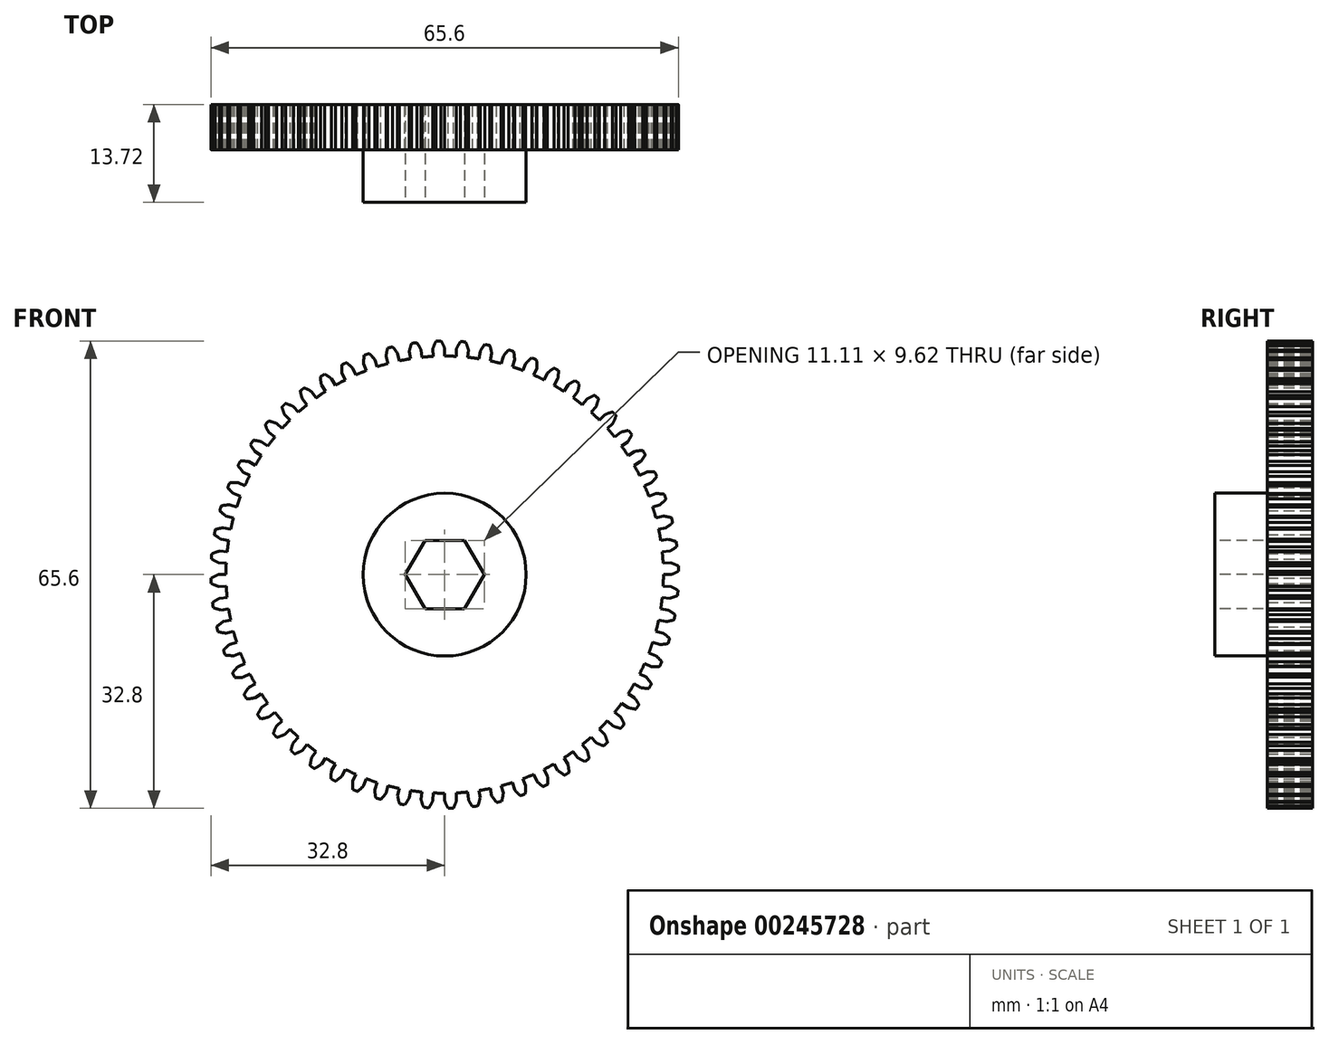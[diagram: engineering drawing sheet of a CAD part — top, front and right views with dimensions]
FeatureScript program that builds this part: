
annotation { "Feature Type Name" : "Feature", "Feature Type Description" : "" }
export const myFeature = defineFeature(function(context is Context, id is Id, definition is map)
    precondition{}
    {
        {
            var Q0;
            Q0=qCreatedBy(makeId("Front.planeOp"),FACE);
            var sketch = newSketch(context, id + "F0", { "sketchPlane" : qUnion([Q0])});
            skCircle(sketch, "E0", {"center": v(0, 0) * mm, "radius": 30.7 * mm});
            skLineSegment(sketch, "E1", {"start": v(0, 30.7) * mm, "end": v(0, 31.75) * mm});
            skLineSegment(sketch, "E2", {"start": v(-0.8, 30.68) * mm, "end": v(-0.86, 32.8) * mm, "construction": true});
            skArc(sketch, "E3.trimOffspring", {"start": v(-0.5, 32.8) * mm, "mid": v(-0.68, 32.8) * mm, "end": v(-0.86, 32.8) * mm});
            skArc(sketch, "E4.trimOffspring", {"start": v(0, 31.75) * mm, "mid": v(-0.23, 32.29) * mm, "end": v(-0.5, 32.8) * mm});
            skArc(sketch, "E5.MirrorCS", {"start": v(-1.22, 32.79) * mm, "mid": v(-1.04, 32.8) * mm, "end": v(-0.86, 32.8) * mm});
            skArc(sketch, "E6.MirrorCS", {"start": v(-1.66, 31.7) * mm, "mid": v(-1.46, 32.25) * mm, "end": v(-1.22, 32.79) * mm});
            skLineSegment(sketch, "E7.MirrorCS", {"start": v(-1.6, 30.65) * mm, "end": v(-1.66, 31.7) * mm});
            skLineSegment(sketch, "E8.1.0", {"start": v(-4, 30.43) * mm, "end": v(-4.28, 32.53) * mm, "construction": true});
            skLineSegment(sketch, "E8.1.1", {"start": v(-3.2, 30.52) * mm, "end": v(-3.32, 31.58) * mm});
            skLineSegment(sketch, "E8.1.2", {"start": v(-4.8, 30.31) * mm, "end": v(-4.97, 31.36) * mm});
            skArc(sketch, "E8.1.3", {"start": v(-4.97, 31.36) * mm, "mid": v(-4.82, 31.92) * mm, "end": v(-4.64, 32.48) * mm});
            skArc(sketch, "E8.1.4", {"start": v(-3.32, 31.58) * mm, "mid": v(-3.6, 32.09) * mm, "end": v(-3.92, 32.57) * mm});
            skArc(sketch, "E8.1.5", {"start": v(-3.92, 32.57) * mm, "mid": v(-4.1, 32.55) * mm, "end": v(-4.28, 32.53) * mm});
            skArc(sketch, "E8.1.6", {"start": v(-4.64, 32.48) * mm, "mid": v(-4.46, 32.5) * mm, "end": v(-4.28, 32.53) * mm});
            skLineSegment(sketch, "E8.2.0", {"start": v(-7.16, 29.84) * mm, "end": v(-7.66, 31.9) * mm, "construction": true});
            skLineSegment(sketch, "E8.2.1", {"start": v(-6.38, 30.02) * mm, "end": v(-6.6, 31.06) * mm});
            skLineSegment(sketch, "E8.2.2", {"start": v(-7.94, 29.65) * mm, "end": v(-8.22, 30.67) * mm});
            skArc(sketch, "E8.2.3", {"start": v(-8.22, 30.67) * mm, "mid": v(-8.13, 31.25) * mm, "end": v(-8.01, 31.82) * mm});
            skArc(sketch, "E8.2.4", {"start": v(-6.6, 31.06) * mm, "mid": v(-6.94, 31.53) * mm, "end": v(-7.3, 31.98) * mm});
            skArc(sketch, "E8.2.5", {"start": v(-7.3, 31.98) * mm, "mid": v(-7.48, 31.94) * mm, "end": v(-7.66, 31.9) * mm});
            skArc(sketch, "E8.2.6", {"start": v(-8.01, 31.82) * mm, "mid": v(-7.83, 31.86) * mm, "end": v(-7.66, 31.9) * mm});
            skLineSegment(sketch, "E9.3.3.0", {"start": v(-9.48, 29.19) * mm, "end": v(-9.81, 30.2) * mm});
            skLineSegment(sketch, "E9.6.3.0", {"start": v(-11, 28.65) * mm, "end": v(-11.38, 29.64) * mm});
            skArc(sketch, "E9.9.3.0", {"start": v(-11.38, 29.64) * mm, "mid": v(-11.36, 30.22) * mm, "end": v(-11.3, 30.8) * mm});
            skArc(sketch, "E9.13.3.0", {"start": v(-9.81, 30.2) * mm, "mid": v(-10.2, 30.64) * mm, "end": v(-10.61, 31.05) * mm});
            skLineSegment(sketch, "E9.14.3.0", {"start": v(-10.25, 28.93) * mm, "end": v(-10.95, 30.93) * mm, "construction": true});
            skArc(sketch, "E9.17.3.0", {"start": v(-10.61, 31.05) * mm, "mid": v(-10.78, 30.99) * mm, "end": v(-10.95, 30.93) * mm});
            skArc(sketch, "E9.21.3.0", {"start": v(-11.3, 30.8) * mm, "mid": v(-11.12, 30.87) * mm, "end": v(-10.95, 30.93) * mm});
            skLineSegment(sketch, "E9.3.4.0", {"start": v(-12.48, 28.04) * mm, "end": v(-12.91, 29) * mm});
            skLineSegment(sketch, "E9.6.4.0", {"start": v(-13.93, 27.35) * mm, "end": v(-14.41, 28.29) * mm});
            skArc(sketch, "E9.9.4.0", {"start": v(-14.41, 28.29) * mm, "mid": v(-14.45, 28.87) * mm, "end": v(-14.45, 29.45) * mm});
            skArc(sketch, "E9.13.4.0", {"start": v(-12.91, 29) * mm, "mid": v(-13.34, 29.4) * mm, "end": v(-13.8, 29.77) * mm});
            skLineSegment(sketch, "E9.14.4.0", {"start": v(-13.21, 27.7) * mm, "end": v(-14.12, 29.61) * mm, "construction": true});
            skArc(sketch, "E9.17.4.0", {"start": v(-13.8, 29.77) * mm, "mid": v(-13.96, 29.69) * mm, "end": v(-14.12, 29.61) * mm});
            skArc(sketch, "E9.21.4.0", {"start": v(-14.45, 29.45) * mm, "mid": v(-14.29, 29.53) * mm, "end": v(-14.12, 29.61) * mm});
            skLineSegment(sketch, "E9.3.5.0", {"start": v(-15.35, 26.58) * mm, "end": v(-15.87, 27.5) * mm});
            skLineSegment(sketch, "E9.6.5.0", {"start": v(-16.72, 25.74) * mm, "end": v(-17.3, 26.63) * mm});
            skArc(sketch, "E9.9.5.0", {"start": v(-17.3, 26.63) * mm, "mid": v(-17.4, 27.2) * mm, "end": v(-17.45, 27.78) * mm});
            skArc(sketch, "E9.13.5.0", {"start": v(-15.88, 27.5) * mm, "mid": v(-16.34, 27.85) * mm, "end": v(-16.83, 28.16) * mm});
            skLineSegment(sketch, "E9.14.5.0", {"start": v(-16.04, 26.17) * mm, "end": v(-17.14, 27.97) * mm, "construction": true});
            skArc(sketch, "E9.17.5.0", {"start": v(-16.83, 28.16) * mm, "mid": v(-16.99, 28.07) * mm, "end": v(-17.14, 27.97) * mm});
            skArc(sketch, "E9.21.5.0", {"start": v(-17.45, 27.78) * mm, "mid": v(-17.3, 27.88) * mm, "end": v(-17.14, 27.97) * mm});
            skLineSegment(sketch, "E9.3.6.0", {"start": v(-18.04, 24.83) * mm, "end": v(-18.66, 25.69) * mm});
            skLineSegment(sketch, "E9.6.6.0", {"start": v(-19.31, 23.85) * mm, "end": v(-19.98, 24.67) * mm});
            skArc(sketch, "E9.9.6.0", {"start": v(-19.98, 24.67) * mm, "mid": v(-20.14, 25.24) * mm, "end": v(-20.26, 25.8) * mm});
            skArc(sketch, "E9.13.6.0", {"start": v(-18.66, 25.69) * mm, "mid": v(-19.16, 25.99) * mm, "end": v(-19.68, 26.25) * mm});
            skLineSegment(sketch, "E9.14.6.0", {"start": v(-18.68, 24.35) * mm, "end": v(-19.97, 26.03) * mm, "construction": true});
            skArc(sketch, "E9.17.6.0", {"start": v(-19.68, 26.25) * mm, "mid": v(-19.83, 26.14) * mm, "end": v(-19.97, 26.03) * mm});
            skArc(sketch, "E9.21.6.0", {"start": v(-20.26, 25.8) * mm, "mid": v(-20.12, 25.92) * mm, "end": v(-19.97, 26.03) * mm});
            skLineSegment(sketch, "E9.3.7.0", {"start": v(-20.54, 22.8) * mm, "end": v(-21.24, 23.6) * mm});
            skLineSegment(sketch, "E9.6.7.0", {"start": v(-21.7, 21.7) * mm, "end": v(-22.45, 22.45) * mm});
            skArc(sketch, "E9.9.7.0", {"start": v(-22.45, 22.45) * mm, "mid": v(-22.67, 23) * mm, "end": v(-22.84, 23.55) * mm});
            skArc(sketch, "E9.13.7.0", {"start": v(-21.24, 23.6) * mm, "mid": v(-21.77, 23.84) * mm, "end": v(-22.32, 24.05) * mm});
            skLineSegment(sketch, "E9.14.7.0", {"start": v(-21.13, 22.26) * mm, "end": v(-22.58, 23.8) * mm, "construction": true});
            skArc(sketch, "E9.17.7.0", {"start": v(-22.32, 24.05) * mm, "mid": v(-22.45, 23.92) * mm, "end": v(-22.58, 23.8) * mm});
            skArc(sketch, "E9.21.7.0", {"start": v(-22.84, 23.55) * mm, "mid": v(-22.71, 23.67) * mm, "end": v(-22.58, 23.8) * mm});
            skLineSegment(sketch, "E9.3.8.0", {"start": v(-22.8, 20.54) * mm, "end": v(-23.6, 21.24) * mm});
            skLineSegment(sketch, "E9.6.8.0", {"start": v(-23.85, 19.31) * mm, "end": v(-24.67, 19.98) * mm});
            skArc(sketch, "E9.9.8.0", {"start": v(-24.67, 19.98) * mm, "mid": v(-24.95, 20.5) * mm, "end": v(-25.18, 21.03) * mm});
            skArc(sketch, "E9.13.8.0", {"start": v(-23.6, 21.24) * mm, "mid": v(-24.15, 21.43) * mm, "end": v(-24.71, 21.58) * mm});
            skLineSegment(sketch, "E9.14.8.0", {"start": v(-23.34, 19.93) * mm, "end": v(-24.95, 21.3) * mm, "construction": true});
            skArc(sketch, "E9.17.8.0", {"start": v(-24.71, 21.58) * mm, "mid": v(-24.83, 21.44) * mm, "end": v(-24.95, 21.3) * mm});
            skArc(sketch, "E9.21.8.0", {"start": v(-25.18, 21.03) * mm, "mid": v(-25.06, 21.17) * mm, "end": v(-24.95, 21.3) * mm});
            skLineSegment(sketch, "E9.3.9.0", {"start": v(-24.83, 18.04) * mm, "end": v(-25.69, 18.66) * mm});
            skLineSegment(sketch, "E9.6.9.0", {"start": v(-25.74, 16.72) * mm, "end": v(-26.63, 17.3) * mm});
            skArc(sketch, "E9.9.9.0", {"start": v(-26.63, 17.3) * mm, "mid": v(-26.95, 17.78) * mm, "end": v(-27.24, 18.28) * mm});
            skArc(sketch, "E9.13.9.0", {"start": v(-25.69, 18.66) * mm, "mid": v(-26.26, 18.8) * mm, "end": v(-26.83, 18.88) * mm});
            skLineSegment(sketch, "E9.14.9.0", {"start": v(-25.3, 17.38) * mm, "end": v(-27.04, 18.58) * mm, "construction": true});
            skArc(sketch, "E9.17.9.0", {"start": v(-26.83, 18.88) * mm, "mid": v(-26.94, 18.73) * mm, "end": v(-27.04, 18.58) * mm});
            skArc(sketch, "E9.21.9.0", {"start": v(-27.24, 18.28) * mm, "mid": v(-27.14, 18.43) * mm, "end": v(-27.04, 18.58) * mm});
            skLineSegment(sketch, "E9.3.10.0", {"start": v(-26.58, 15.35) * mm, "end": v(-27.5, 15.88) * mm});
            skLineSegment(sketch, "E9.6.10.0", {"start": v(-27.35, 13.93) * mm, "end": v(-28.29, 14.41) * mm});
            skArc(sketch, "E9.9.10.0", {"start": v(-28.29, 14.41) * mm, "mid": v(-28.66, 14.86) * mm, "end": v(-29, 15.34) * mm});
            skArc(sketch, "E9.13.10.0", {"start": v(-27.5, 15.88) * mm, "mid": v(-28.08, 15.94) * mm, "end": v(-28.66, 15.97) * mm});
            skLineSegment(sketch, "E9.14.10.0", {"start": v(-26.97, 14.64) * mm, "end": v(-28.83, 15.65) * mm, "construction": true});
            skArc(sketch, "E9.17.10.0", {"start": v(-28.66, 15.97) * mm, "mid": v(-28.75, 15.81) * mm, "end": v(-28.83, 15.65) * mm});
            skArc(sketch, "E9.21.10.0", {"start": v(-29, 15.34) * mm, "mid": v(-28.92, 15.5) * mm, "end": v(-28.83, 15.65) * mm});
            skLineSegment(sketch, "E9.3.11.0", {"start": v(-28.04, 12.48) * mm, "end": v(-29, 12.91) * mm});
            skLineSegment(sketch, "E9.6.11.0", {"start": v(-28.65, 11) * mm, "end": v(-29.64, 11.38) * mm});
            skArc(sketch, "E9.9.11.0", {"start": v(-29.64, 11.38) * mm, "mid": v(-30.06, 11.78) * mm, "end": v(-30.45, 12.22) * mm});
            skArc(sketch, "E9.13.11.0", {"start": v(-29, 12.91) * mm, "mid": v(-29.59, 12.92) * mm, "end": v(-30.17, 12.89) * mm});
            skLineSegment(sketch, "E9.14.11.0", {"start": v(-28.36, 11.75) * mm, "end": v(-30.31, 12.56) * mm, "construction": true});
            skArc(sketch, "E9.17.11.0", {"start": v(-30.17, 12.89) * mm, "mid": v(-30.24, 12.72) * mm, "end": v(-30.31, 12.56) * mm});
            skArc(sketch, "E9.21.11.0", {"start": v(-30.45, 12.22) * mm, "mid": v(-30.38, 12.39) * mm, "end": v(-30.31, 12.56) * mm});
            skLineSegment(sketch, "E9.3.12.0", {"start": v(-29.19, 9.48) * mm, "end": v(-30.2, 9.81) * mm});
            skLineSegment(sketch, "E9.6.12.0", {"start": v(-29.65, 7.94) * mm, "end": v(-30.67, 8.22) * mm});
            skArc(sketch, "E9.9.12.0", {"start": v(-30.67, 8.22) * mm, "mid": v(-31.13, 8.58) * mm, "end": v(-31.56, 8.97) * mm});
            skArc(sketch, "E9.13.12.0", {"start": v(-30.2, 9.81) * mm, "mid": v(-30.78, 9.76) * mm, "end": v(-31.35, 9.66) * mm});
            skLineSegment(sketch, "E9.14.12.0", {"start": v(-29.43, 8.72) * mm, "end": v(-31.46, 9.32) * mm, "construction": true});
            skArc(sketch, "E9.17.12.0", {"start": v(-31.35, 9.66) * mm, "mid": v(-31.4, 9.5) * mm, "end": v(-31.46, 9.32) * mm});
            skArc(sketch, "E9.21.12.0", {"start": v(-31.56, 8.97) * mm, "mid": v(-31.5, 9.14) * mm, "end": v(-31.46, 9.32) * mm});
            skLineSegment(sketch, "E9.3.13.0", {"start": v(-30.02, 6.38) * mm, "end": v(-31.06, 6.6) * mm});
            skLineSegment(sketch, "E9.6.13.0", {"start": v(-30.31, 4.8) * mm, "end": v(-31.36, 4.97) * mm});
            skArc(sketch, "E9.9.13.0", {"start": v(-31.36, 4.97) * mm, "mid": v(-31.85, 5.28) * mm, "end": v(-32.32, 5.62) * mm});
            skArc(sketch, "E9.13.13.0", {"start": v(-31.06, 6.6) * mm, "mid": v(-31.63, 6.49) * mm, "end": v(-32.2, 6.33) * mm});
            skLineSegment(sketch, "E9.14.13.0", {"start": v(-30.18, 5.6) * mm, "end": v(-32.26, 5.98) * mm, "construction": true});
            skArc(sketch, "E9.17.13.0", {"start": v(-32.2, 6.33) * mm, "mid": v(-32.23, 6.16) * mm, "end": v(-32.26, 5.98) * mm});
            skArc(sketch, "E9.21.13.0", {"start": v(-32.32, 5.62) * mm, "mid": v(-32.3, 5.8) * mm, "end": v(-32.26, 5.98) * mm});
            skLineSegment(sketch, "E9.3.14.0", {"start": v(-30.52, 3.2) * mm, "end": v(-31.58, 3.32) * mm});
            skLineSegment(sketch, "E9.6.14.0", {"start": v(-30.65, 1.6) * mm, "end": v(-31.7, 1.66) * mm});
            skArc(sketch, "E9.9.14.0", {"start": v(-31.7, 1.66) * mm, "mid": v(-32.23, 1.92) * mm, "end": v(-32.73, 2.21) * mm});
            skArc(sketch, "E9.13.14.0", {"start": v(-31.58, 3.32) * mm, "mid": v(-32.13, 3.15) * mm, "end": v(-32.68, 2.93) * mm});
            skLineSegment(sketch, "E9.14.14.0", {"start": v(-30.6, 2.4) * mm, "end": v(-32.7, 2.57) * mm, "construction": true});
            skArc(sketch, "E9.17.14.0", {"start": v(-32.68, 2.93) * mm, "mid": v(-32.7, 2.75) * mm, "end": v(-32.7, 2.57) * mm});
            skArc(sketch, "E9.21.14.0", {"start": v(-32.73, 2.21) * mm, "mid": v(-32.72, 2.4) * mm, "end": v(-32.7, 2.57) * mm});
            skLineSegment(sketch, "E9.3.15.0", {"start": v(-30.7, 0) * mm, "end": v(-31.75, 0) * mm});
            skLineSegment(sketch, "E9.6.15.0", {"start": v(-30.65, -1.6) * mm, "end": v(-31.7, -1.66) * mm});
            skArc(sketch, "E9.9.15.0", {"start": v(-31.7, -1.66) * mm, "mid": v(-32.25, -1.46) * mm, "end": v(-32.79, -1.22) * mm});
            skArc(sketch, "E9.13.15.0", {"start": v(-31.75, 0) * mm, "mid": v(-32.29, -0.23) * mm, "end": v(-32.8, -0.5) * mm});
            skLineSegment(sketch, "E9.14.15.0", {"start": v(-30.68, -0.8) * mm, "end": v(-32.8, -0.86) * mm, "construction": true});
            skArc(sketch, "E9.17.15.0", {"start": v(-32.8, -0.5) * mm, "mid": v(-32.8, -0.68) * mm, "end": v(-32.8, -0.86) * mm});
            skArc(sketch, "E9.21.15.0", {"start": v(-32.79, -1.22) * mm, "mid": v(-32.8, -1.04) * mm, "end": v(-32.8, -0.86) * mm});
            skLineSegment(sketch, "E9.3.16.0", {"start": v(-30.52, -3.2) * mm, "end": v(-31.58, -3.32) * mm});
            skLineSegment(sketch, "E9.6.16.0", {"start": v(-30.31, -4.8) * mm, "end": v(-31.36, -4.97) * mm});
            skArc(sketch, "E9.9.16.0", {"start": v(-31.36, -4.97) * mm, "mid": v(-31.92, -4.82) * mm, "end": v(-32.48, -4.64) * mm});
            skArc(sketch, "E9.13.16.0", {"start": v(-31.58, -3.32) * mm, "mid": v(-32.09, -3.6) * mm, "end": v(-32.57, -3.92) * mm});
            skLineSegment(sketch, "E9.14.16.0", {"start": v(-30.43, -4) * mm, "end": v(-32.53, -4.28) * mm, "construction": true});
            skArc(sketch, "E9.17.16.0", {"start": v(-32.57, -3.92) * mm, "mid": v(-32.55, -4.1) * mm, "end": v(-32.53, -4.28) * mm});
            skArc(sketch, "E9.21.16.0", {"start": v(-32.48, -4.64) * mm, "mid": v(-32.5, -4.46) * mm, "end": v(-32.53, -4.28) * mm});
            skLineSegment(sketch, "E9.3.17.0", {"start": v(-30.02, -6.38) * mm, "end": v(-31.06, -6.6) * mm});
            skLineSegment(sketch, "E9.6.17.0", {"start": v(-29.65, -7.94) * mm, "end": v(-30.67, -8.22) * mm});
            skArc(sketch, "E9.9.17.0", {"start": v(-30.67, -8.22) * mm, "mid": v(-31.25, -8.13) * mm, "end": v(-31.82, -8.01) * mm});
            skArc(sketch, "E9.13.17.0", {"start": v(-31.06, -6.6) * mm, "mid": v(-31.53, -6.94) * mm, "end": v(-31.98, -7.3) * mm});
            skLineSegment(sketch, "E9.14.17.0", {"start": v(-29.84, -7.16) * mm, "end": v(-31.9, -7.66) * mm, "construction": true});
            skArc(sketch, "E9.17.17.0", {"start": v(-31.98, -7.3) * mm, "mid": v(-31.94, -7.48) * mm, "end": v(-31.9, -7.66) * mm});
            skArc(sketch, "E9.21.17.0", {"start": v(-31.82, -8.01) * mm, "mid": v(-31.86, -7.83) * mm, "end": v(-31.9, -7.66) * mm});
            skLineSegment(sketch, "E9.3.18.0", {"start": v(-29.19, -9.48) * mm, "end": v(-30.2, -9.81) * mm});
            skLineSegment(sketch, "E9.6.18.0", {"start": v(-28.65, -11) * mm, "end": v(-29.64, -11.38) * mm});
            skArc(sketch, "E9.9.18.0", {"start": v(-29.64, -11.38) * mm, "mid": v(-30.22, -11.36) * mm, "end": v(-30.8, -11.3) * mm});
            skArc(sketch, "E9.13.18.0", {"start": v(-30.2, -9.81) * mm, "mid": v(-30.64, -10.2) * mm, "end": v(-31.05, -10.61) * mm});
            skLineSegment(sketch, "E9.14.18.0", {"start": v(-28.93, -10.25) * mm, "end": v(-30.93, -10.95) * mm, "construction": true});
            skArc(sketch, "E9.17.18.0", {"start": v(-31.05, -10.61) * mm, "mid": v(-30.99, -10.78) * mm, "end": v(-30.93, -10.95) * mm});
            skArc(sketch, "E9.21.18.0", {"start": v(-30.8, -11.3) * mm, "mid": v(-30.87, -11.12) * mm, "end": v(-30.93, -10.95) * mm});
            skLineSegment(sketch, "E9.3.19.0", {"start": v(-28.04, -12.48) * mm, "end": v(-29, -12.91) * mm});
            skLineSegment(sketch, "E9.6.19.0", {"start": v(-27.35, -13.93) * mm, "end": v(-28.29, -14.41) * mm});
            skArc(sketch, "E9.9.19.0", {"start": v(-28.29, -14.41) * mm, "mid": v(-28.87, -14.45) * mm, "end": v(-29.45, -14.45) * mm});
            skArc(sketch, "E9.13.19.0", {"start": v(-29, -12.91) * mm, "mid": v(-29.4, -13.34) * mm, "end": v(-29.77, -13.8) * mm});
            skLineSegment(sketch, "E9.14.19.0", {"start": v(-27.7, -13.21) * mm, "end": v(-29.61, -14.12) * mm, "construction": true});
            skArc(sketch, "E9.17.19.0", {"start": v(-29.77, -13.8) * mm, "mid": v(-29.69, -13.96) * mm, "end": v(-29.61, -14.12) * mm});
            skArc(sketch, "E9.21.19.0", {"start": v(-29.45, -14.45) * mm, "mid": v(-29.53, -14.29) * mm, "end": v(-29.61, -14.12) * mm});
            skLineSegment(sketch, "E9.3.20.0", {"start": v(-26.58, -15.35) * mm, "end": v(-27.5, -15.88) * mm});
            skLineSegment(sketch, "E9.6.20.0", {"start": v(-25.74, -16.72) * mm, "end": v(-26.63, -17.3) * mm});
            skArc(sketch, "E9.9.20.0", {"start": v(-26.63, -17.3) * mm, "mid": v(-27.2, -17.4) * mm, "end": v(-27.78, -17.45) * mm});
            skArc(sketch, "E9.13.20.0", {"start": v(-27.5, -15.87) * mm, "mid": v(-27.85, -16.34) * mm, "end": v(-28.16, -16.83) * mm});
            skLineSegment(sketch, "E9.14.20.0", {"start": v(-26.17, -16.04) * mm, "end": v(-27.97, -17.14) * mm, "construction": true});
            skArc(sketch, "E9.17.20.0", {"start": v(-28.16, -16.83) * mm, "mid": v(-28.07, -16.99) * mm, "end": v(-27.97, -17.14) * mm});
            skArc(sketch, "E9.21.20.0", {"start": v(-27.78, -17.45) * mm, "mid": v(-27.88, -17.3) * mm, "end": v(-27.97, -17.14) * mm});
            skLineSegment(sketch, "E9.3.21.0", {"start": v(-24.83, -18.04) * mm, "end": v(-25.69, -18.66) * mm});
            skLineSegment(sketch, "E9.6.21.0", {"start": v(-23.85, -19.31) * mm, "end": v(-24.67, -19.98) * mm});
            skArc(sketch, "E9.9.21.0", {"start": v(-24.67, -19.98) * mm, "mid": v(-25.24, -20.14) * mm, "end": v(-25.8, -20.26) * mm});
            skArc(sketch, "E9.13.21.0", {"start": v(-25.69, -18.66) * mm, "mid": v(-25.99, -19.16) * mm, "end": v(-26.25, -19.68) * mm});
            skLineSegment(sketch, "E9.14.21.0", {"start": v(-24.35, -18.68) * mm, "end": v(-26.03, -19.97) * mm, "construction": true});
            skArc(sketch, "E9.17.21.0", {"start": v(-26.25, -19.68) * mm, "mid": v(-26.14, -19.83) * mm, "end": v(-26.03, -19.97) * mm});
            skArc(sketch, "E9.21.21.0", {"start": v(-25.8, -20.26) * mm, "mid": v(-25.92, -20.12) * mm, "end": v(-26.03, -19.97) * mm});
            skLineSegment(sketch, "E9.3.22.0", {"start": v(-22.8, -20.54) * mm, "end": v(-23.6, -21.24) * mm});
            skLineSegment(sketch, "E9.6.22.0", {"start": v(-21.7, -21.7) * mm, "end": v(-22.45, -22.45) * mm});
            skArc(sketch, "E9.9.22.0", {"start": v(-22.45, -22.45) * mm, "mid": v(-23, -22.67) * mm, "end": v(-23.55, -22.84) * mm});
            skArc(sketch, "E9.13.22.0", {"start": v(-23.6, -21.24) * mm, "mid": v(-23.84, -21.77) * mm, "end": v(-24.05, -22.32) * mm});
            skLineSegment(sketch, "E9.14.22.0", {"start": v(-22.26, -21.13) * mm, "end": v(-23.8, -22.58) * mm, "construction": true});
            skArc(sketch, "E9.17.22.0", {"start": v(-24.05, -22.32) * mm, "mid": v(-23.92, -22.45) * mm, "end": v(-23.8, -22.58) * mm});
            skArc(sketch, "E9.21.22.0", {"start": v(-23.55, -22.84) * mm, "mid": v(-23.67, -22.71) * mm, "end": v(-23.8, -22.58) * mm});
            skLineSegment(sketch, "E9.3.23.0", {"start": v(-20.54, -22.8) * mm, "end": v(-21.24, -23.6) * mm});
            skLineSegment(sketch, "E9.6.23.0", {"start": v(-19.31, -23.85) * mm, "end": v(-19.98, -24.67) * mm});
            skArc(sketch, "E9.9.23.0", {"start": v(-19.98, -24.67) * mm, "mid": v(-20.5, -24.95) * mm, "end": v(-21.03, -25.18) * mm});
            skArc(sketch, "E9.13.23.0", {"start": v(-21.24, -23.6) * mm, "mid": v(-21.43, -24.15) * mm, "end": v(-21.58, -24.71) * mm});
            skLineSegment(sketch, "E9.14.23.0", {"start": v(-19.93, -23.34) * mm, "end": v(-21.3, -24.95) * mm, "construction": true});
            skArc(sketch, "E9.17.23.0", {"start": v(-21.58, -24.71) * mm, "mid": v(-21.44, -24.83) * mm, "end": v(-21.3, -24.95) * mm});
            skArc(sketch, "E9.21.23.0", {"start": v(-21.03, -25.18) * mm, "mid": v(-21.17, -25.06) * mm, "end": v(-21.3, -24.95) * mm});
            skLineSegment(sketch, "E9.3.24.0", {"start": v(-18.04, -24.83) * mm, "end": v(-18.66, -25.69) * mm});
            skLineSegment(sketch, "E9.6.24.0", {"start": v(-16.72, -25.74) * mm, "end": v(-17.3, -26.63) * mm});
            skArc(sketch, "E9.9.24.0", {"start": v(-17.3, -26.63) * mm, "mid": v(-17.78, -26.95) * mm, "end": v(-18.28, -27.24) * mm});
            skArc(sketch, "E9.13.24.0", {"start": v(-18.66, -25.69) * mm, "mid": v(-18.8, -26.26) * mm, "end": v(-18.88, -26.83) * mm});
            skLineSegment(sketch, "E9.14.24.0", {"start": v(-17.38, -25.3) * mm, "end": v(-18.58, -27.04) * mm, "construction": true});
            skArc(sketch, "E9.17.24.0", {"start": v(-18.88, -26.83) * mm, "mid": v(-18.73, -26.94) * mm, "end": v(-18.58, -27.04) * mm});
            skArc(sketch, "E9.21.24.0", {"start": v(-18.28, -27.24) * mm, "mid": v(-18.43, -27.14) * mm, "end": v(-18.58, -27.04) * mm});
            skLineSegment(sketch, "E9.3.25.0", {"start": v(-15.35, -26.58) * mm, "end": v(-15.87, -27.5) * mm});
            skLineSegment(sketch, "E9.6.25.0", {"start": v(-13.93, -27.35) * mm, "end": v(-14.41, -28.29) * mm});
            skArc(sketch, "E9.9.25.0", {"start": v(-14.41, -28.29) * mm, "mid": v(-14.86, -28.66) * mm, "end": v(-15.34, -29) * mm});
            skArc(sketch, "E9.13.25.0", {"start": v(-15.87, -27.5) * mm, "mid": v(-15.94, -28.08) * mm, "end": v(-15.97, -28.66) * mm});
            skLineSegment(sketch, "E9.14.25.0", {"start": v(-14.64, -26.97) * mm, "end": v(-15.65, -28.83) * mm, "construction": true});
            skArc(sketch, "E9.17.25.0", {"start": v(-15.97, -28.66) * mm, "mid": v(-15.81, -28.75) * mm, "end": v(-15.65, -28.83) * mm});
            skArc(sketch, "E9.21.25.0", {"start": v(-15.34, -29) * mm, "mid": v(-15.5, -28.92) * mm, "end": v(-15.65, -28.83) * mm});
            skLineSegment(sketch, "E9.3.26.0", {"start": v(-12.48, -28.04) * mm, "end": v(-12.91, -29) * mm});
            skLineSegment(sketch, "E9.6.26.0", {"start": v(-11, -28.65) * mm, "end": v(-11.38, -29.64) * mm});
            skArc(sketch, "E9.9.26.0", {"start": v(-11.38, -29.64) * mm, "mid": v(-11.78, -30.06) * mm, "end": v(-12.22, -30.45) * mm});
            skArc(sketch, "E9.13.26.0", {"start": v(-12.91, -29) * mm, "mid": v(-12.92, -29.59) * mm, "end": v(-12.89, -30.17) * mm});
            skLineSegment(sketch, "E9.14.26.0", {"start": v(-11.75, -28.36) * mm, "end": v(-12.56, -30.31) * mm, "construction": true});
            skArc(sketch, "E9.17.26.0", {"start": v(-12.89, -30.17) * mm, "mid": v(-12.72, -30.24) * mm, "end": v(-12.56, -30.31) * mm});
            skArc(sketch, "E9.21.26.0", {"start": v(-12.22, -30.45) * mm, "mid": v(-12.39, -30.38) * mm, "end": v(-12.56, -30.31) * mm});
            skLineSegment(sketch, "E9.3.27.0", {"start": v(-9.48, -29.19) * mm, "end": v(-9.81, -30.2) * mm});
            skLineSegment(sketch, "E9.6.27.0", {"start": v(-7.94, -29.65) * mm, "end": v(-8.22, -30.67) * mm});
            skArc(sketch, "E9.9.27.0", {"start": v(-8.22, -30.67) * mm, "mid": v(-8.58, -31.13) * mm, "end": v(-8.97, -31.56) * mm});
            skArc(sketch, "E9.13.27.0", {"start": v(-9.81, -30.2) * mm, "mid": v(-9.76, -30.78) * mm, "end": v(-9.66, -31.35) * mm});
            skLineSegment(sketch, "E9.14.27.0", {"start": v(-8.72, -29.43) * mm, "end": v(-9.32, -31.46) * mm, "construction": true});
            skArc(sketch, "E9.17.27.0", {"start": v(-9.66, -31.35) * mm, "mid": v(-9.5, -31.4) * mm, "end": v(-9.32, -31.46) * mm});
            skArc(sketch, "E9.21.27.0", {"start": v(-8.97, -31.56) * mm, "mid": v(-9.14, -31.5) * mm, "end": v(-9.32, -31.46) * mm});
            skLineSegment(sketch, "E9.3.28.0", {"start": v(-6.38, -30.02) * mm, "end": v(-6.6, -31.06) * mm});
            skLineSegment(sketch, "E9.6.28.0", {"start": v(-4.8, -30.31) * mm, "end": v(-4.97, -31.36) * mm});
            skArc(sketch, "E9.9.28.0", {"start": v(-4.97, -31.36) * mm, "mid": v(-5.28, -31.85) * mm, "end": v(-5.62, -32.32) * mm});
            skArc(sketch, "E9.13.28.0", {"start": v(-6.6, -31.06) * mm, "mid": v(-6.49, -31.63) * mm, "end": v(-6.33, -32.2) * mm});
            skLineSegment(sketch, "E9.14.28.0", {"start": v(-5.6, -30.18) * mm, "end": v(-5.98, -32.26) * mm, "construction": true});
            skArc(sketch, "E9.17.28.0", {"start": v(-6.33, -32.2) * mm, "mid": v(-6.16, -32.23) * mm, "end": v(-5.98, -32.26) * mm});
            skArc(sketch, "E9.21.28.0", {"start": v(-5.62, -32.32) * mm, "mid": v(-5.8, -32.3) * mm, "end": v(-5.98, -32.26) * mm});
            skLineSegment(sketch, "E9.3.29.0", {"start": v(-3.2, -30.52) * mm, "end": v(-3.32, -31.58) * mm});
            skLineSegment(sketch, "E9.6.29.0", {"start": v(-1.6, -30.65) * mm, "end": v(-1.66, -31.7) * mm});
            skArc(sketch, "E9.9.29.0", {"start": v(-1.66, -31.7) * mm, "mid": v(-1.92, -32.23) * mm, "end": v(-2.21, -32.73) * mm});
            skArc(sketch, "E9.13.29.0", {"start": v(-3.32, -31.58) * mm, "mid": v(-3.15, -32.13) * mm, "end": v(-2.93, -32.68) * mm});
            skLineSegment(sketch, "E9.14.29.0", {"start": v(-2.4, -30.6) * mm, "end": v(-2.57, -32.7) * mm, "construction": true});
            skArc(sketch, "E9.17.29.0", {"start": v(-2.93, -32.68) * mm, "mid": v(-2.75, -32.7) * mm, "end": v(-2.57, -32.7) * mm});
            skArc(sketch, "E9.21.29.0", {"start": v(-2.21, -32.73) * mm, "mid": v(-2.4, -32.72) * mm, "end": v(-2.57, -32.7) * mm});
            skLineSegment(sketch, "E9.3.30.0", {"start": v(0, -30.7) * mm, "end": v(0, -31.75) * mm});
            skLineSegment(sketch, "E9.6.30.0", {"start": v(1.6, -30.65) * mm, "end": v(1.66, -31.7) * mm});
            skArc(sketch, "E9.9.30.0", {"start": v(1.66, -31.7) * mm, "mid": v(1.46, -32.25) * mm, "end": v(1.22, -32.79) * mm});
            skArc(sketch, "E9.13.30.0", {"start": v(0, -31.75) * mm, "mid": v(0.23, -32.29) * mm, "end": v(0.5, -32.8) * mm});
            skLineSegment(sketch, "E9.14.30.0", {"start": v(0.8, -30.68) * mm, "end": v(0.86, -32.8) * mm, "construction": true});
            skArc(sketch, "E9.17.30.0", {"start": v(0.5, -32.8) * mm, "mid": v(0.68, -32.8) * mm, "end": v(0.86, -32.8) * mm});
            skArc(sketch, "E9.21.30.0", {"start": v(1.22, -32.79) * mm, "mid": v(1.04, -32.8) * mm, "end": v(0.86, -32.8) * mm});
            skLineSegment(sketch, "E9.3.31.0", {"start": v(3.2, -30.52) * mm, "end": v(3.32, -31.58) * mm});
            skLineSegment(sketch, "E9.6.31.0", {"start": v(4.8, -30.31) * mm, "end": v(4.97, -31.36) * mm});
            skArc(sketch, "E9.9.31.0", {"start": v(4.97, -31.36) * mm, "mid": v(4.82, -31.92) * mm, "end": v(4.64, -32.48) * mm});
            skArc(sketch, "E9.13.31.0", {"start": v(3.32, -31.58) * mm, "mid": v(3.6, -32.09) * mm, "end": v(3.92, -32.57) * mm});
            skLineSegment(sketch, "E9.14.31.0", {"start": v(4, -30.43) * mm, "end": v(4.28, -32.53) * mm, "construction": true});
            skArc(sketch, "E9.17.31.0", {"start": v(3.92, -32.57) * mm, "mid": v(4.1, -32.55) * mm, "end": v(4.28, -32.53) * mm});
            skArc(sketch, "E9.21.31.0", {"start": v(4.64, -32.48) * mm, "mid": v(4.46, -32.5) * mm, "end": v(4.28, -32.53) * mm});
            skLineSegment(sketch, "E9.3.32.0", {"start": v(6.38, -30.02) * mm, "end": v(6.6, -31.06) * mm});
            skLineSegment(sketch, "E9.6.32.0", {"start": v(7.94, -29.65) * mm, "end": v(8.22, -30.67) * mm});
            skArc(sketch, "E9.9.32.0", {"start": v(8.22, -30.67) * mm, "mid": v(8.13, -31.25) * mm, "end": v(8.01, -31.82) * mm});
            skArc(sketch, "E9.13.32.0", {"start": v(6.6, -31.06) * mm, "mid": v(6.94, -31.53) * mm, "end": v(7.3, -31.98) * mm});
            skLineSegment(sketch, "E9.14.32.0", {"start": v(7.16, -29.84) * mm, "end": v(7.66, -31.9) * mm, "construction": true});
            skArc(sketch, "E9.17.32.0", {"start": v(7.3, -31.98) * mm, "mid": v(7.48, -31.94) * mm, "end": v(7.66, -31.9) * mm});
            skArc(sketch, "E9.21.32.0", {"start": v(8.01, -31.82) * mm, "mid": v(7.83, -31.86) * mm, "end": v(7.66, -31.9) * mm});
            skLineSegment(sketch, "E9.3.33.0", {"start": v(9.48, -29.19) * mm, "end": v(9.81, -30.2) * mm});
            skLineSegment(sketch, "E9.6.33.0", {"start": v(11, -28.65) * mm, "end": v(11.38, -29.64) * mm});
            skArc(sketch, "E9.9.33.0", {"start": v(11.38, -29.64) * mm, "mid": v(11.36, -30.22) * mm, "end": v(11.3, -30.8) * mm});
            skArc(sketch, "E9.13.33.0", {"start": v(9.81, -30.2) * mm, "mid": v(10.2, -30.64) * mm, "end": v(10.61, -31.05) * mm});
            skLineSegment(sketch, "E9.14.33.0", {"start": v(10.25, -28.93) * mm, "end": v(10.95, -30.93) * mm, "construction": true});
            skArc(sketch, "E9.17.33.0", {"start": v(10.61, -31.05) * mm, "mid": v(10.78, -30.99) * mm, "end": v(10.95, -30.93) * mm});
            skArc(sketch, "E9.21.33.0", {"start": v(11.3, -30.8) * mm, "mid": v(11.12, -30.87) * mm, "end": v(10.95, -30.93) * mm});
            skLineSegment(sketch, "E9.3.34.0", {"start": v(12.48, -28.04) * mm, "end": v(12.91, -29) * mm});
            skLineSegment(sketch, "E9.6.34.0", {"start": v(13.93, -27.35) * mm, "end": v(14.41, -28.29) * mm});
            skArc(sketch, "E9.9.34.0", {"start": v(14.41, -28.29) * mm, "mid": v(14.45, -28.87) * mm, "end": v(14.45, -29.45) * mm});
            skArc(sketch, "E9.13.34.0", {"start": v(12.91, -29) * mm, "mid": v(13.34, -29.4) * mm, "end": v(13.8, -29.77) * mm});
            skLineSegment(sketch, "E9.14.34.0", {"start": v(13.21, -27.7) * mm, "end": v(14.12, -29.61) * mm, "construction": true});
            skArc(sketch, "E9.17.34.0", {"start": v(13.8, -29.77) * mm, "mid": v(13.96, -29.69) * mm, "end": v(14.12, -29.61) * mm});
            skArc(sketch, "E9.21.34.0", {"start": v(14.45, -29.45) * mm, "mid": v(14.29, -29.53) * mm, "end": v(14.12, -29.61) * mm});
            skLineSegment(sketch, "E9.3.35.0", {"start": v(15.35, -26.58) * mm, "end": v(15.87, -27.5) * mm});
            skLineSegment(sketch, "E9.6.35.0", {"start": v(16.72, -25.74) * mm, "end": v(17.3, -26.63) * mm});
            skArc(sketch, "E9.9.35.0", {"start": v(17.3, -26.63) * mm, "mid": v(17.4, -27.2) * mm, "end": v(17.45, -27.78) * mm});
            skArc(sketch, "E9.13.35.0", {"start": v(15.87, -27.5) * mm, "mid": v(16.34, -27.85) * mm, "end": v(16.83, -28.16) * mm});
            skLineSegment(sketch, "E9.14.35.0", {"start": v(16.04, -26.17) * mm, "end": v(17.14, -27.97) * mm, "construction": true});
            skArc(sketch, "E9.17.35.0", {"start": v(16.83, -28.16) * mm, "mid": v(16.99, -28.07) * mm, "end": v(17.14, -27.97) * mm});
            skArc(sketch, "E9.21.35.0", {"start": v(17.45, -27.78) * mm, "mid": v(17.3, -27.88) * mm, "end": v(17.14, -27.97) * mm});
            skLineSegment(sketch, "E9.3.36.0", {"start": v(18.04, -24.83) * mm, "end": v(18.66, -25.69) * mm});
            skLineSegment(sketch, "E9.6.36.0", {"start": v(19.31, -23.85) * mm, "end": v(19.98, -24.67) * mm});
            skArc(sketch, "E9.9.36.0", {"start": v(19.98, -24.67) * mm, "mid": v(20.14, -25.24) * mm, "end": v(20.26, -25.8) * mm});
            skArc(sketch, "E9.13.36.0", {"start": v(18.66, -25.69) * mm, "mid": v(19.16, -25.99) * mm, "end": v(19.68, -26.25) * mm});
            skLineSegment(sketch, "E9.14.36.0", {"start": v(18.68, -24.35) * mm, "end": v(19.97, -26.03) * mm, "construction": true});
            skArc(sketch, "E9.17.36.0", {"start": v(19.68, -26.25) * mm, "mid": v(19.83, -26.14) * mm, "end": v(19.97, -26.03) * mm});
            skArc(sketch, "E9.21.36.0", {"start": v(20.26, -25.8) * mm, "mid": v(20.12, -25.92) * mm, "end": v(19.97, -26.03) * mm});
            skLineSegment(sketch, "E9.3.37.0", {"start": v(20.54, -22.8) * mm, "end": v(21.24, -23.6) * mm});
            skLineSegment(sketch, "E9.6.37.0", {"start": v(21.7, -21.7) * mm, "end": v(22.45, -22.45) * mm});
            skArc(sketch, "E9.9.37.0", {"start": v(22.45, -22.45) * mm, "mid": v(22.67, -23) * mm, "end": v(22.84, -23.55) * mm});
            skArc(sketch, "E9.13.37.0", {"start": v(21.24, -23.6) * mm, "mid": v(21.77, -23.84) * mm, "end": v(22.32, -24.05) * mm});
            skLineSegment(sketch, "E9.14.37.0", {"start": v(21.13, -22.26) * mm, "end": v(22.58, -23.8) * mm, "construction": true});
            skArc(sketch, "E9.17.37.0", {"start": v(22.32, -24.05) * mm, "mid": v(22.45, -23.92) * mm, "end": v(22.58, -23.8) * mm});
            skArc(sketch, "E9.21.37.0", {"start": v(22.84, -23.55) * mm, "mid": v(22.71, -23.67) * mm, "end": v(22.58, -23.8) * mm});
            skLineSegment(sketch, "E9.3.38.0", {"start": v(22.8, -20.54) * mm, "end": v(23.6, -21.24) * mm});
            skLineSegment(sketch, "E9.6.38.0", {"start": v(23.85, -19.31) * mm, "end": v(24.67, -19.98) * mm});
            skArc(sketch, "E9.9.38.0", {"start": v(24.67, -19.98) * mm, "mid": v(24.95, -20.5) * mm, "end": v(25.18, -21.03) * mm});
            skArc(sketch, "E9.13.38.0", {"start": v(23.6, -21.24) * mm, "mid": v(24.15, -21.43) * mm, "end": v(24.71, -21.58) * mm});
            skLineSegment(sketch, "E9.14.38.0", {"start": v(23.34, -19.93) * mm, "end": v(24.95, -21.3) * mm, "construction": true});
            skArc(sketch, "E9.17.38.0", {"start": v(24.71, -21.58) * mm, "mid": v(24.83, -21.44) * mm, "end": v(24.95, -21.3) * mm});
            skArc(sketch, "E9.21.38.0", {"start": v(25.18, -21.03) * mm, "mid": v(25.06, -21.17) * mm, "end": v(24.95, -21.3) * mm});
            skLineSegment(sketch, "E9.3.39.0", {"start": v(24.83, -18.04) * mm, "end": v(25.69, -18.66) * mm});
            skLineSegment(sketch, "E9.6.39.0", {"start": v(25.74, -16.72) * mm, "end": v(26.63, -17.3) * mm});
            skArc(sketch, "E9.9.39.0", {"start": v(26.63, -17.3) * mm, "mid": v(26.95, -17.78) * mm, "end": v(27.24, -18.28) * mm});
            skArc(sketch, "E9.13.39.0", {"start": v(25.69, -18.66) * mm, "mid": v(26.26, -18.8) * mm, "end": v(26.83, -18.88) * mm});
            skLineSegment(sketch, "E9.14.39.0", {"start": v(25.3, -17.38) * mm, "end": v(27.04, -18.58) * mm, "construction": true});
            skArc(sketch, "E9.17.39.0", {"start": v(26.83, -18.88) * mm, "mid": v(26.94, -18.73) * mm, "end": v(27.04, -18.58) * mm});
            skArc(sketch, "E9.21.39.0", {"start": v(27.24, -18.28) * mm, "mid": v(27.14, -18.43) * mm, "end": v(27.04, -18.58) * mm});
            skLineSegment(sketch, "E9.3.40.0", {"start": v(26.58, -15.35) * mm, "end": v(27.5, -15.88) * mm});
            skLineSegment(sketch, "E9.6.40.0", {"start": v(27.35, -13.93) * mm, "end": v(28.29, -14.41) * mm});
            skArc(sketch, "E9.9.40.0", {"start": v(28.29, -14.41) * mm, "mid": v(28.66, -14.86) * mm, "end": v(29, -15.34) * mm});
            skArc(sketch, "E9.13.40.0", {"start": v(27.5, -15.88) * mm, "mid": v(28.08, -15.94) * mm, "end": v(28.66, -15.97) * mm});
            skLineSegment(sketch, "E9.14.40.0", {"start": v(26.97, -14.64) * mm, "end": v(28.83, -15.65) * mm, "construction": true});
            skArc(sketch, "E9.17.40.0", {"start": v(28.66, -15.97) * mm, "mid": v(28.75, -15.81) * mm, "end": v(28.83, -15.65) * mm});
            skArc(sketch, "E9.21.40.0", {"start": v(29, -15.34) * mm, "mid": v(28.92, -15.5) * mm, "end": v(28.83, -15.65) * mm});
            skLineSegment(sketch, "E9.3.41.0", {"start": v(28.04, -12.48) * mm, "end": v(29, -12.91) * mm});
            skLineSegment(sketch, "E9.6.41.0", {"start": v(28.65, -11) * mm, "end": v(29.64, -11.38) * mm});
            skArc(sketch, "E9.9.41.0", {"start": v(29.64, -11.38) * mm, "mid": v(30.06, -11.78) * mm, "end": v(30.45, -12.22) * mm});
            skArc(sketch, "E9.13.41.0", {"start": v(29, -12.91) * mm, "mid": v(29.59, -12.92) * mm, "end": v(30.17, -12.89) * mm});
            skLineSegment(sketch, "E9.14.41.0", {"start": v(28.36, -11.75) * mm, "end": v(30.31, -12.56) * mm, "construction": true});
            skArc(sketch, "E9.17.41.0", {"start": v(30.17, -12.89) * mm, "mid": v(30.24, -12.72) * mm, "end": v(30.31, -12.56) * mm});
            skArc(sketch, "E9.21.41.0", {"start": v(30.45, -12.22) * mm, "mid": v(30.38, -12.39) * mm, "end": v(30.31, -12.56) * mm});
            skLineSegment(sketch, "E9.3.42.0", {"start": v(29.19, -9.48) * mm, "end": v(30.2, -9.81) * mm});
            skLineSegment(sketch, "E9.6.42.0", {"start": v(29.65, -7.94) * mm, "end": v(30.67, -8.22) * mm});
            skArc(sketch, "E9.9.42.0", {"start": v(30.67, -8.22) * mm, "mid": v(31.13, -8.58) * mm, "end": v(31.56, -8.97) * mm});
            skArc(sketch, "E9.13.42.0", {"start": v(30.2, -9.81) * mm, "mid": v(30.78, -9.76) * mm, "end": v(31.35, -9.66) * mm});
            skLineSegment(sketch, "E9.14.42.0", {"start": v(29.43, -8.72) * mm, "end": v(31.46, -9.32) * mm, "construction": true});
            skArc(sketch, "E9.17.42.0", {"start": v(31.35, -9.66) * mm, "mid": v(31.4, -9.5) * mm, "end": v(31.46, -9.32) * mm});
            skArc(sketch, "E9.21.42.0", {"start": v(31.56, -8.97) * mm, "mid": v(31.5, -9.14) * mm, "end": v(31.46, -9.32) * mm});
            skLineSegment(sketch, "E9.3.43.0", {"start": v(30.02, -6.38) * mm, "end": v(31.06, -6.6) * mm});
            skLineSegment(sketch, "E9.6.43.0", {"start": v(30.31, -4.8) * mm, "end": v(31.36, -4.97) * mm});
            skArc(sketch, "E9.9.43.0", {"start": v(31.36, -4.97) * mm, "mid": v(31.85, -5.28) * mm, "end": v(32.32, -5.62) * mm});
            skArc(sketch, "E9.13.43.0", {"start": v(31.06, -6.6) * mm, "mid": v(31.63, -6.49) * mm, "end": v(32.2, -6.33) * mm});
            skLineSegment(sketch, "E9.14.43.0", {"start": v(30.18, -5.6) * mm, "end": v(32.26, -5.98) * mm, "construction": true});
            skArc(sketch, "E9.17.43.0", {"start": v(32.2, -6.33) * mm, "mid": v(32.23, -6.16) * mm, "end": v(32.26, -5.98) * mm});
            skArc(sketch, "E9.21.43.0", {"start": v(32.32, -5.62) * mm, "mid": v(32.3, -5.8) * mm, "end": v(32.26, -5.98) * mm});
            skLineSegment(sketch, "E9.3.44.0", {"start": v(30.52, -3.2) * mm, "end": v(31.58, -3.32) * mm});
            skLineSegment(sketch, "E9.6.44.0", {"start": v(30.65, -1.6) * mm, "end": v(31.7, -1.66) * mm});
            skArc(sketch, "E9.9.44.0", {"start": v(31.7, -1.66) * mm, "mid": v(32.23, -1.92) * mm, "end": v(32.73, -2.21) * mm});
            skArc(sketch, "E9.13.44.0", {"start": v(31.58, -3.32) * mm, "mid": v(32.13, -3.15) * mm, "end": v(32.68, -2.93) * mm});
            skLineSegment(sketch, "E9.14.44.0", {"start": v(30.6, -2.4) * mm, "end": v(32.7, -2.57) * mm, "construction": true});
            skArc(sketch, "E9.17.44.0", {"start": v(32.68, -2.93) * mm, "mid": v(32.7, -2.75) * mm, "end": v(32.7, -2.57) * mm});
            skArc(sketch, "E9.21.44.0", {"start": v(32.73, -2.21) * mm, "mid": v(32.72, -2.4) * mm, "end": v(32.7, -2.57) * mm});
            skLineSegment(sketch, "E9.3.45.0", {"start": v(30.7, 0) * mm, "end": v(31.75, 0) * mm});
            skLineSegment(sketch, "E9.6.45.0", {"start": v(30.65, 1.6) * mm, "end": v(31.7, 1.66) * mm});
            skArc(sketch, "E9.9.45.0", {"start": v(31.7, 1.66) * mm, "mid": v(32.25, 1.46) * mm, "end": v(32.79, 1.22) * mm});
            skArc(sketch, "E9.13.45.0", {"start": v(31.75, 0) * mm, "mid": v(32.29, 0.23) * mm, "end": v(32.8, 0.5) * mm});
            skLineSegment(sketch, "E9.14.45.0", {"start": v(30.68, 0.8) * mm, "end": v(32.8, 0.86) * mm, "construction": true});
            skArc(sketch, "E9.17.45.0", {"start": v(32.8, 0.5) * mm, "mid": v(32.8, 0.68) * mm, "end": v(32.8, 0.86) * mm});
            skArc(sketch, "E9.21.45.0", {"start": v(32.79, 1.22) * mm, "mid": v(32.8, 1.04) * mm, "end": v(32.8, 0.86) * mm});
            skLineSegment(sketch, "E9.3.46.0", {"start": v(30.52, 3.2) * mm, "end": v(31.58, 3.32) * mm});
            skLineSegment(sketch, "E9.6.46.0", {"start": v(30.31, 4.8) * mm, "end": v(31.36, 4.97) * mm});
            skArc(sketch, "E9.9.46.0", {"start": v(31.36, 4.97) * mm, "mid": v(31.92, 4.82) * mm, "end": v(32.48, 4.64) * mm});
            skArc(sketch, "E9.13.46.0", {"start": v(31.58, 3.32) * mm, "mid": v(32.09, 3.6) * mm, "end": v(32.57, 3.92) * mm});
            skLineSegment(sketch, "E9.14.46.0", {"start": v(30.43, 4) * mm, "end": v(32.53, 4.28) * mm, "construction": true});
            skArc(sketch, "E9.17.46.0", {"start": v(32.57, 3.92) * mm, "mid": v(32.55, 4.1) * mm, "end": v(32.53, 4.28) * mm});
            skArc(sketch, "E9.21.46.0", {"start": v(32.48, 4.64) * mm, "mid": v(32.5, 4.46) * mm, "end": v(32.53, 4.28) * mm});
            skLineSegment(sketch, "E9.3.47.0", {"start": v(30.02, 6.38) * mm, "end": v(31.06, 6.6) * mm});
            skLineSegment(sketch, "E9.6.47.0", {"start": v(29.65, 7.94) * mm, "end": v(30.67, 8.22) * mm});
            skArc(sketch, "E9.9.47.0", {"start": v(30.67, 8.22) * mm, "mid": v(31.25, 8.13) * mm, "end": v(31.82, 8.01) * mm});
            skArc(sketch, "E9.13.47.0", {"start": v(31.06, 6.6) * mm, "mid": v(31.53, 6.94) * mm, "end": v(31.98, 7.3) * mm});
            skLineSegment(sketch, "E9.14.47.0", {"start": v(29.84, 7.16) * mm, "end": v(31.9, 7.66) * mm, "construction": true});
            skArc(sketch, "E9.17.47.0", {"start": v(31.98, 7.3) * mm, "mid": v(31.94, 7.48) * mm, "end": v(31.9, 7.66) * mm});
            skArc(sketch, "E9.21.47.0", {"start": v(31.82, 8.01) * mm, "mid": v(31.86, 7.83) * mm, "end": v(31.9, 7.66) * mm});
            skLineSegment(sketch, "E9.3.48.0", {"start": v(29.19, 9.48) * mm, "end": v(30.2, 9.81) * mm});
            skLineSegment(sketch, "E9.6.48.0", {"start": v(28.65, 11) * mm, "end": v(29.64, 11.38) * mm});
            skArc(sketch, "E9.9.48.0", {"start": v(29.64, 11.38) * mm, "mid": v(30.22, 11.36) * mm, "end": v(30.8, 11.3) * mm});
            skArc(sketch, "E9.13.48.0", {"start": v(30.2, 9.81) * mm, "mid": v(30.64, 10.2) * mm, "end": v(31.05, 10.61) * mm});
            skLineSegment(sketch, "E9.14.48.0", {"start": v(28.93, 10.25) * mm, "end": v(30.93, 10.95) * mm, "construction": true});
            skArc(sketch, "E9.17.48.0", {"start": v(31.05, 10.61) * mm, "mid": v(30.99, 10.78) * mm, "end": v(30.93, 10.95) * mm});
            skArc(sketch, "E9.21.48.0", {"start": v(30.8, 11.3) * mm, "mid": v(30.87, 11.12) * mm, "end": v(30.93, 10.95) * mm});
            skLineSegment(sketch, "E9.3.49.0", {"start": v(28.04, 12.48) * mm, "end": v(29, 12.91) * mm});
            skLineSegment(sketch, "E9.6.49.0", {"start": v(27.35, 13.93) * mm, "end": v(28.29, 14.41) * mm});
            skArc(sketch, "E9.9.49.0", {"start": v(28.29, 14.41) * mm, "mid": v(28.87, 14.45) * mm, "end": v(29.45, 14.45) * mm});
            skArc(sketch, "E9.13.49.0", {"start": v(29, 12.91) * mm, "mid": v(29.4, 13.34) * mm, "end": v(29.77, 13.8) * mm});
            skLineSegment(sketch, "E9.14.49.0", {"start": v(27.7, 13.21) * mm, "end": v(29.61, 14.12) * mm, "construction": true});
            skArc(sketch, "E9.17.49.0", {"start": v(29.77, 13.8) * mm, "mid": v(29.69, 13.96) * mm, "end": v(29.61, 14.12) * mm});
            skArc(sketch, "E9.21.49.0", {"start": v(29.45, 14.45) * mm, "mid": v(29.53, 14.29) * mm, "end": v(29.61, 14.12) * mm});
            skLineSegment(sketch, "E9.3.50.0", {"start": v(26.58, 15.35) * mm, "end": v(27.5, 15.88) * mm});
            skLineSegment(sketch, "E9.6.50.0", {"start": v(25.74, 16.72) * mm, "end": v(26.63, 17.3) * mm});
            skArc(sketch, "E9.9.50.0", {"start": v(26.63, 17.3) * mm, "mid": v(27.2, 17.4) * mm, "end": v(27.78, 17.45) * mm});
            skArc(sketch, "E9.13.50.0", {"start": v(27.5, 15.88) * mm, "mid": v(27.85, 16.34) * mm, "end": v(28.16, 16.83) * mm});
            skLineSegment(sketch, "E9.14.50.0", {"start": v(26.17, 16.04) * mm, "end": v(27.97, 17.14) * mm, "construction": true});
            skArc(sketch, "E9.17.50.0", {"start": v(28.16, 16.83) * mm, "mid": v(28.07, 16.99) * mm, "end": v(27.97, 17.14) * mm});
            skArc(sketch, "E9.21.50.0", {"start": v(27.78, 17.45) * mm, "mid": v(27.88, 17.3) * mm, "end": v(27.97, 17.14) * mm});
            skLineSegment(sketch, "E9.3.51.0", {"start": v(24.83, 18.04) * mm, "end": v(25.69, 18.66) * mm});
            skLineSegment(sketch, "E9.6.51.0", {"start": v(23.85, 19.31) * mm, "end": v(24.67, 19.98) * mm});
            skArc(sketch, "E9.9.51.0", {"start": v(24.67, 19.98) * mm, "mid": v(25.24, 20.14) * mm, "end": v(25.8, 20.26) * mm});
            skArc(sketch, "E9.13.51.0", {"start": v(25.69, 18.66) * mm, "mid": v(25.99, 19.16) * mm, "end": v(26.25, 19.68) * mm});
            skLineSegment(sketch, "E9.14.51.0", {"start": v(24.35, 18.68) * mm, "end": v(26.03, 19.97) * mm, "construction": true});
            skArc(sketch, "E9.17.51.0", {"start": v(26.25, 19.68) * mm, "mid": v(26.14, 19.83) * mm, "end": v(26.03, 19.97) * mm});
            skArc(sketch, "E9.21.51.0", {"start": v(25.8, 20.26) * mm, "mid": v(25.92, 20.12) * mm, "end": v(26.03, 19.97) * mm});
            skLineSegment(sketch, "E9.3.52.0", {"start": v(22.8, 20.54) * mm, "end": v(23.6, 21.24) * mm});
            skLineSegment(sketch, "E9.6.52.0", {"start": v(21.7, 21.7) * mm, "end": v(22.45, 22.45) * mm});
            skArc(sketch, "E9.9.52.0", {"start": v(22.45, 22.45) * mm, "mid": v(23, 22.67) * mm, "end": v(23.55, 22.84) * mm});
            skArc(sketch, "E9.13.52.0", {"start": v(23.6, 21.24) * mm, "mid": v(23.84, 21.77) * mm, "end": v(24.05, 22.32) * mm});
            skLineSegment(sketch, "E9.14.52.0", {"start": v(22.26, 21.13) * mm, "end": v(23.8, 22.58) * mm, "construction": true});
            skArc(sketch, "E9.17.52.0", {"start": v(24.05, 22.32) * mm, "mid": v(23.92, 22.45) * mm, "end": v(23.8, 22.58) * mm});
            skArc(sketch, "E9.21.52.0", {"start": v(23.55, 22.84) * mm, "mid": v(23.67, 22.71) * mm, "end": v(23.8, 22.58) * mm});
            skLineSegment(sketch, "E9.3.53.0", {"start": v(20.54, 22.8) * mm, "end": v(21.24, 23.6) * mm});
            skLineSegment(sketch, "E9.6.53.0", {"start": v(19.31, 23.85) * mm, "end": v(19.98, 24.67) * mm});
            skArc(sketch, "E9.9.53.0", {"start": v(19.98, 24.67) * mm, "mid": v(20.5, 24.95) * mm, "end": v(21.03, 25.18) * mm});
            skArc(sketch, "E9.13.53.0", {"start": v(21.24, 23.6) * mm, "mid": v(21.43, 24.15) * mm, "end": v(21.58, 24.71) * mm});
            skLineSegment(sketch, "E9.14.53.0", {"start": v(19.93, 23.34) * mm, "end": v(21.3, 24.95) * mm, "construction": true});
            skArc(sketch, "E9.17.53.0", {"start": v(21.58, 24.71) * mm, "mid": v(21.44, 24.83) * mm, "end": v(21.3, 24.95) * mm});
            skArc(sketch, "E9.21.53.0", {"start": v(21.03, 25.18) * mm, "mid": v(21.17, 25.06) * mm, "end": v(21.3, 24.95) * mm});
            skLineSegment(sketch, "E9.3.54.0", {"start": v(18.04, 24.83) * mm, "end": v(18.66, 25.69) * mm});
            skLineSegment(sketch, "E9.6.54.0", {"start": v(16.72, 25.74) * mm, "end": v(17.3, 26.63) * mm});
            skArc(sketch, "E9.9.54.0", {"start": v(17.3, 26.63) * mm, "mid": v(17.78, 26.95) * mm, "end": v(18.28, 27.24) * mm});
            skArc(sketch, "E9.13.54.0", {"start": v(18.66, 25.69) * mm, "mid": v(18.8, 26.26) * mm, "end": v(18.88, 26.83) * mm});
            skLineSegment(sketch, "E9.14.54.0", {"start": v(17.38, 25.3) * mm, "end": v(18.58, 27.04) * mm, "construction": true});
            skArc(sketch, "E9.17.54.0", {"start": v(18.88, 26.83) * mm, "mid": v(18.73, 26.94) * mm, "end": v(18.58, 27.04) * mm});
            skArc(sketch, "E9.21.54.0", {"start": v(18.28, 27.24) * mm, "mid": v(18.43, 27.14) * mm, "end": v(18.58, 27.04) * mm});
            skLineSegment(sketch, "E9.3.55.0", {"start": v(15.35, 26.58) * mm, "end": v(15.87, 27.5) * mm});
            skLineSegment(sketch, "E9.6.55.0", {"start": v(13.93, 27.35) * mm, "end": v(14.41, 28.29) * mm});
            skArc(sketch, "E9.9.55.0", {"start": v(14.41, 28.29) * mm, "mid": v(14.86, 28.66) * mm, "end": v(15.34, 29) * mm});
            skArc(sketch, "E9.13.55.0", {"start": v(15.87, 27.5) * mm, "mid": v(15.94, 28.08) * mm, "end": v(15.97, 28.66) * mm});
            skLineSegment(sketch, "E9.14.55.0", {"start": v(14.64, 26.97) * mm, "end": v(15.65, 28.83) * mm, "construction": true});
            skArc(sketch, "E9.17.55.0", {"start": v(15.97, 28.66) * mm, "mid": v(15.81, 28.75) * mm, "end": v(15.65, 28.83) * mm});
            skArc(sketch, "E9.21.55.0", {"start": v(15.34, 29) * mm, "mid": v(15.5, 28.92) * mm, "end": v(15.65, 28.83) * mm});
            skLineSegment(sketch, "E9.3.56.0", {"start": v(12.48, 28.04) * mm, "end": v(12.91, 29) * mm});
            skLineSegment(sketch, "E9.6.56.0", {"start": v(11, 28.65) * mm, "end": v(11.38, 29.64) * mm});
            skArc(sketch, "E9.9.56.0", {"start": v(11.38, 29.64) * mm, "mid": v(11.78, 30.06) * mm, "end": v(12.22, 30.45) * mm});
            skArc(sketch, "E9.13.56.0", {"start": v(12.91, 29) * mm, "mid": v(12.92, 29.59) * mm, "end": v(12.89, 30.17) * mm});
            skLineSegment(sketch, "E9.14.56.0", {"start": v(11.75, 28.36) * mm, "end": v(12.56, 30.31) * mm, "construction": true});
            skArc(sketch, "E9.17.56.0", {"start": v(12.89, 30.17) * mm, "mid": v(12.72, 30.24) * mm, "end": v(12.56, 30.31) * mm});
            skArc(sketch, "E9.21.56.0", {"start": v(12.22, 30.45) * mm, "mid": v(12.39, 30.38) * mm, "end": v(12.56, 30.31) * mm});
            skLineSegment(sketch, "E9.3.57.0", {"start": v(9.48, 29.19) * mm, "end": v(9.81, 30.2) * mm});
            skLineSegment(sketch, "E9.6.57.0", {"start": v(7.94, 29.65) * mm, "end": v(8.22, 30.67) * mm});
            skArc(sketch, "E9.9.57.0", {"start": v(8.22, 30.67) * mm, "mid": v(8.58, 31.13) * mm, "end": v(8.97, 31.56) * mm});
            skArc(sketch, "E9.13.57.0", {"start": v(9.81, 30.2) * mm, "mid": v(9.76, 30.78) * mm, "end": v(9.66, 31.35) * mm});
            skLineSegment(sketch, "E9.14.57.0", {"start": v(8.72, 29.43) * mm, "end": v(9.32, 31.46) * mm, "construction": true});
            skArc(sketch, "E9.17.57.0", {"start": v(9.66, 31.35) * mm, "mid": v(9.5, 31.4) * mm, "end": v(9.32, 31.46) * mm});
            skArc(sketch, "E9.21.57.0", {"start": v(8.97, 31.56) * mm, "mid": v(9.14, 31.5) * mm, "end": v(9.32, 31.46) * mm});
            skLineSegment(sketch, "E9.3.58.0", {"start": v(6.38, 30.02) * mm, "end": v(6.6, 31.06) * mm});
            skLineSegment(sketch, "E9.6.58.0", {"start": v(4.8, 30.31) * mm, "end": v(4.97, 31.36) * mm});
            skArc(sketch, "E9.9.58.0", {"start": v(4.97, 31.36) * mm, "mid": v(5.28, 31.85) * mm, "end": v(5.62, 32.32) * mm});
            skArc(sketch, "E9.13.58.0", {"start": v(6.6, 31.06) * mm, "mid": v(6.49, 31.63) * mm, "end": v(6.33, 32.2) * mm});
            skLineSegment(sketch, "E9.14.58.0", {"start": v(5.6, 30.18) * mm, "end": v(5.98, 32.26) * mm, "construction": true});
            skArc(sketch, "E9.17.58.0", {"start": v(6.33, 32.2) * mm, "mid": v(6.16, 32.23) * mm, "end": v(5.98, 32.26) * mm});
            skArc(sketch, "E9.21.58.0", {"start": v(5.62, 32.32) * mm, "mid": v(5.8, 32.3) * mm, "end": v(5.98, 32.26) * mm});
            skLineSegment(sketch, "E9.3.59.0", {"start": v(3.2, 30.52) * mm, "end": v(3.32, 31.58) * mm});
            skLineSegment(sketch, "E9.6.59.0", {"start": v(1.6, 30.65) * mm, "end": v(1.66, 31.7) * mm});
            skArc(sketch, "E9.9.59.0", {"start": v(1.66, 31.7) * mm, "mid": v(1.92, 32.23) * mm, "end": v(2.21, 32.73) * mm});
            skArc(sketch, "E9.13.59.0", {"start": v(3.32, 31.58) * mm, "mid": v(3.15, 32.13) * mm, "end": v(2.93, 32.68) * mm});
            skLineSegment(sketch, "E9.14.59.0", {"start": v(2.4, 30.6) * mm, "end": v(2.57, 32.7) * mm, "construction": true});
            skArc(sketch, "E9.17.59.0", {"start": v(2.93, 32.68) * mm, "mid": v(2.75, 32.7) * mm, "end": v(2.57, 32.7) * mm});
            skArc(sketch, "E9.21.59.0", {"start": v(2.21, 32.73) * mm, "mid": v(2.4, 32.72) * mm, "end": v(2.57, 32.7) * mm});
            skSolve(sketch);
        }
        {
            var Q0;
            {var subQ0=sQuery(id+"F0.wireOp",EDGE,"E0");var subQ27=makeQuery(id+"F0.imprint","INTERSECT",VERTEX,{"derivedFrom":[subQ0,sQuery(id+"F0.wireOp",EDGE,"E9.3.45.0")]});Q0=makeQuery(id+"F0.imprint","IMPRINT",FACE,{"disambiguationData":[TD([[makeQuery(id+"F0.imprint","IMPRINT",EDGE,{"disambiguationData":[TD([[subQ27,-1.0]])],"derivedFrom":subQ0}),1.0]])]});}
            var Q1;
            {var subQ1=sQuery(id+"F0.wireOp",EDGE,"E9.3.30.0");Q1=makeQuery(id+"F0.imprint","IMPRINT",FACE,{"disambiguationData":[TD([[makeQuery(id+"F0.imprint","IMPRINT",EDGE,{"derivedFrom":subQ1}),1.0]])]});}
            var Q2;
            {var subQ1=sQuery(id+"F0.wireOp",EDGE,"E9.3.14.0");Q2=makeQuery(id+"F0.imprint","IMPRINT",FACE,{"disambiguationData":[TD([[makeQuery(id+"F0.imprint","IMPRINT",EDGE,{"derivedFrom":subQ1}),1.0]])]});}
            var Q3;
            {var subQ0=sQuery(id+"F0.wireOp",EDGE,"E9.3.15.0");Q3=makeQuery(id+"F0.imprint","IMPRINT",FACE,{"disambiguationData":[TD([[makeQuery(id+"F0.imprint","IMPRINT",EDGE,{"derivedFrom":subQ0}),1.0]])]});}
            var Q4;
            {var subQ1=sQuery(id+"F0.wireOp",EDGE,"E9.3.7.0");Q4=makeQuery(id+"F0.imprint","IMPRINT",FACE,{"disambiguationData":[TD([[makeQuery(id+"F0.imprint","IMPRINT",EDGE,{"derivedFrom":subQ1}),1.0]])]});}
            var Q5;
            {var subQ1=sQuery(id+"F0.wireOp",EDGE,"E9.3.40.0");Q5=makeQuery(id+"F0.imprint","IMPRINT",FACE,{"disambiguationData":[TD([[makeQuery(id+"F0.imprint","IMPRINT",EDGE,{"derivedFrom":subQ1}),1.0]])]});}
            var Q6;
            {var subQ1=sQuery(id+"F0.wireOp",EDGE,"E9.3.24.0");Q6=makeQuery(id+"F0.imprint","IMPRINT",FACE,{"disambiguationData":[TD([[makeQuery(id+"F0.imprint","IMPRINT",EDGE,{"derivedFrom":subQ1}),1.0]])]});}
            var Q7;
            {var subQ1=sQuery(id+"F0.wireOp",EDGE,"E9.3.27.0");Q7=makeQuery(id+"F0.imprint","IMPRINT",FACE,{"disambiguationData":[TD([[makeQuery(id+"F0.imprint","IMPRINT",EDGE,{"derivedFrom":subQ1}),1.0]])]});}
            var Q8;
            {var subQ1=sQuery(id+"F0.wireOp",EDGE,"E9.3.28.0");Q8=makeQuery(id+"F0.imprint","IMPRINT",FACE,{"disambiguationData":[TD([[makeQuery(id+"F0.imprint","IMPRINT",EDGE,{"derivedFrom":subQ1}),1.0]])]});}
            var Q9;
            {var subQ1=sQuery(id+"F0.wireOp",EDGE,"E9.3.12.0");Q9=makeQuery(id+"F0.imprint","IMPRINT",FACE,{"disambiguationData":[TD([[makeQuery(id+"F0.imprint","IMPRINT",EDGE,{"derivedFrom":subQ1}),1.0]])]});}
            var Q10;
            {var subQ1=sQuery(id+"F0.wireOp",EDGE,"E9.3.29.0");Q10=makeQuery(id+"F0.imprint","IMPRINT",FACE,{"disambiguationData":[TD([[makeQuery(id+"F0.imprint","IMPRINT",EDGE,{"derivedFrom":subQ1}),1.0]])]});}
            var Q11;
            {var subQ1=sQuery(id+"F0.wireOp",EDGE,"E9.3.13.0");Q11=makeQuery(id+"F0.imprint","IMPRINT",FACE,{"disambiguationData":[TD([[makeQuery(id+"F0.imprint","IMPRINT",EDGE,{"derivedFrom":subQ1}),1.0]])]});}
            var Q12;
            {var subQ0=sQuery(id+"F0.wireOp",EDGE,"E9.3.53.0");Q12=makeQuery(id+"F0.imprint","IMPRINT",FACE,{"disambiguationData":[TD([[makeQuery(id+"F0.imprint","IMPRINT",EDGE,{"derivedFrom":subQ0}),1.0]])]});}
            var Q13;
            {var subQ1=sQuery(id+"F0.wireOp",EDGE,"E9.3.54.0");Q13=makeQuery(id+"F0.imprint","IMPRINT",FACE,{"disambiguationData":[TD([[makeQuery(id+"F0.imprint","IMPRINT",EDGE,{"derivedFrom":subQ1}),1.0]])]});}
            var Q14;
            {var subQ1=sQuery(id+"F0.wireOp",EDGE,"E9.3.55.0");Q14=makeQuery(id+"F0.imprint","IMPRINT",FACE,{"disambiguationData":[TD([[makeQuery(id+"F0.imprint","IMPRINT",EDGE,{"derivedFrom":subQ1}),1.0]])]});}
            var Q15;
            {var subQ1=sQuery(id+"F0.wireOp",EDGE,"E9.3.16.0");Q15=makeQuery(id+"F0.imprint","IMPRINT",FACE,{"disambiguationData":[TD([[makeQuery(id+"F0.imprint","IMPRINT",EDGE,{"derivedFrom":subQ1}),1.0]])]});}
            var Q16;
            {var subQ1=sQuery(id+"F0.wireOp",EDGE,"E9.3.32.0");Q16=makeQuery(id+"F0.imprint","IMPRINT",FACE,{"disambiguationData":[TD([[makeQuery(id+"F0.imprint","IMPRINT",EDGE,{"derivedFrom":subQ1}),1.0]])]});}
            var Q17;
            {var subQ1=sQuery(id+"F0.wireOp",EDGE,"E9.3.31.0");Q17=makeQuery(id+"F0.imprint","IMPRINT",FACE,{"disambiguationData":[TD([[makeQuery(id+"F0.imprint","IMPRINT",EDGE,{"derivedFrom":subQ1}),1.0]])]});}
            var Q18;
            {var subQ1=sQuery(id+"F0.wireOp",EDGE,"E8.1.1");Q18=makeQuery(id+"F0.imprint","IMPRINT",FACE,{"disambiguationData":[TD([[makeQuery(id+"F0.imprint","IMPRINT",EDGE,{"derivedFrom":subQ1}),1.0]])]});}
            var Q19;
            {var subQ0=sQuery(id+"F0.wireOp",EDGE,"E9.3.33.0");Q19=makeQuery(id+"F0.imprint","IMPRINT",FACE,{"disambiguationData":[TD([[makeQuery(id+"F0.imprint","IMPRINT",EDGE,{"derivedFrom":subQ0}),1.0]])]});}
            var Q20;
            {var subQ1=sQuery(id+"F0.wireOp",EDGE,"E9.3.17.0");Q20=makeQuery(id+"F0.imprint","IMPRINT",FACE,{"disambiguationData":[TD([[makeQuery(id+"F0.imprint","IMPRINT",EDGE,{"derivedFrom":subQ1}),1.0]])]});}
            var Q21;
            {var subQ1=sQuery(id+"F0.wireOp",EDGE,"E8.2.1");Q21=makeQuery(id+"F0.imprint","IMPRINT",FACE,{"disambiguationData":[TD([[makeQuery(id+"F0.imprint","IMPRINT",EDGE,{"derivedFrom":subQ1}),1.0]])]});}
            var Q22;
            {var subQ1=sQuery(id+"F0.wireOp",EDGE,"E9.3.34.0");Q22=makeQuery(id+"F0.imprint","IMPRINT",FACE,{"disambiguationData":[TD([[makeQuery(id+"F0.imprint","IMPRINT",EDGE,{"derivedFrom":subQ1}),1.0]])]});}
            var Q23;
            {var subQ1=sQuery(id+"F0.wireOp",EDGE,"E9.3.3.0");Q23=makeQuery(id+"F0.imprint","IMPRINT",FACE,{"disambiguationData":[TD([[makeQuery(id+"F0.imprint","IMPRINT",EDGE,{"derivedFrom":subQ1}),1.0]])]});}
            var Q24;
            {var subQ1=sQuery(id+"F0.wireOp",EDGE,"E9.3.35.0");Q24=makeQuery(id+"F0.imprint","IMPRINT",FACE,{"disambiguationData":[TD([[makeQuery(id+"F0.imprint","IMPRINT",EDGE,{"derivedFrom":subQ1}),1.0]])]});}
            var Q25;
            {var subQ1=sQuery(id+"F0.wireOp",EDGE,"E9.3.19.0");Q25=makeQuery(id+"F0.imprint","IMPRINT",FACE,{"disambiguationData":[TD([[makeQuery(id+"F0.imprint","IMPRINT",EDGE,{"derivedFrom":subQ1}),1.0]])]});}
            var Q26;
            {var subQ1=sQuery(id+"F0.wireOp",EDGE,"E9.3.4.0");Q26=makeQuery(id+"F0.imprint","IMPRINT",FACE,{"disambiguationData":[TD([[makeQuery(id+"F0.imprint","IMPRINT",EDGE,{"derivedFrom":subQ1}),1.0]])]});}
            var Q27;
            {var subQ1=sQuery(id+"F0.wireOp",EDGE,"E9.3.36.0");Q27=makeQuery(id+"F0.imprint","IMPRINT",FACE,{"disambiguationData":[TD([[makeQuery(id+"F0.imprint","IMPRINT",EDGE,{"derivedFrom":subQ1}),1.0]])]});}
            var Q28;
            {var subQ0=sQuery(id+"F0.wireOp",EDGE,"E9.3.20.0");Q28=makeQuery(id+"F0.imprint","IMPRINT",FACE,{"disambiguationData":[TD([[makeQuery(id+"F0.imprint","IMPRINT",EDGE,{"derivedFrom":subQ0}),1.0]])]});}
            var Q29;
            {var subQ1=sQuery(id+"F0.wireOp",EDGE,"E9.3.5.0");Q29=makeQuery(id+"F0.imprint","IMPRINT",FACE,{"disambiguationData":[TD([[makeQuery(id+"F0.imprint","IMPRINT",EDGE,{"derivedFrom":subQ1}),1.0]])]});}
            var Q30;
            {var subQ1=sQuery(id+"F0.wireOp",EDGE,"E9.3.37.0");Q30=makeQuery(id+"F0.imprint","IMPRINT",FACE,{"disambiguationData":[TD([[makeQuery(id+"F0.imprint","IMPRINT",EDGE,{"derivedFrom":subQ1}),1.0]])]});}
            var Q31;
            {var subQ1=sQuery(id+"F0.wireOp",EDGE,"E9.3.21.0");Q31=makeQuery(id+"F0.imprint","IMPRINT",FACE,{"disambiguationData":[TD([[makeQuery(id+"F0.imprint","IMPRINT",EDGE,{"derivedFrom":subQ1}),1.0]])]});}
            var Q32;
            {var subQ1=sQuery(id+"F0.wireOp",EDGE,"E9.3.6.0");Q32=makeQuery(id+"F0.imprint","IMPRINT",FACE,{"disambiguationData":[TD([[makeQuery(id+"F0.imprint","IMPRINT",EDGE,{"derivedFrom":subQ1}),1.0]])]});}
            var Q33;
            {var subQ1=sQuery(id+"F0.wireOp",EDGE,"E9.3.38.0");Q33=makeQuery(id+"F0.imprint","IMPRINT",FACE,{"disambiguationData":[TD([[makeQuery(id+"F0.imprint","IMPRINT",EDGE,{"derivedFrom":subQ1}),1.0]])]});}
            var Q34;
            {var subQ1=sQuery(id+"F0.wireOp",EDGE,"E9.3.22.0");Q34=makeQuery(id+"F0.imprint","IMPRINT",FACE,{"disambiguationData":[TD([[makeQuery(id+"F0.imprint","IMPRINT",EDGE,{"derivedFrom":subQ1}),1.0]])]});}
            var Q35;
            {var subQ1=sQuery(id+"F0.wireOp",EDGE,"E9.3.39.0");Q35=makeQuery(id+"F0.imprint","IMPRINT",FACE,{"disambiguationData":[TD([[makeQuery(id+"F0.imprint","IMPRINT",EDGE,{"derivedFrom":subQ1}),1.0]])]});}
            var Q36;
            {var subQ1=sQuery(id+"F0.wireOp",EDGE,"E9.3.23.0");Q36=makeQuery(id+"F0.imprint","IMPRINT",FACE,{"disambiguationData":[TD([[makeQuery(id+"F0.imprint","IMPRINT",EDGE,{"derivedFrom":subQ1}),1.0]])]});}
            var Q37;
            {var subQ1=sQuery(id+"F0.wireOp",EDGE,"E9.3.8.0");Q37=makeQuery(id+"F0.imprint","IMPRINT",FACE,{"disambiguationData":[TD([[makeQuery(id+"F0.imprint","IMPRINT",EDGE,{"derivedFrom":subQ1}),1.0]])]});}
            var Q38;
            {var subQ1=sQuery(id+"F0.wireOp",EDGE,"E9.3.41.0");Q38=makeQuery(id+"F0.imprint","IMPRINT",FACE,{"disambiguationData":[TD([[makeQuery(id+"F0.imprint","IMPRINT",EDGE,{"derivedFrom":subQ1}),1.0]])]});}
            var Q39;
            {var subQ0=sQuery(id+"F0.wireOp",EDGE,"E9.3.42.0");Q39=makeQuery(id+"F0.imprint","IMPRINT",FACE,{"disambiguationData":[TD([[makeQuery(id+"F0.imprint","IMPRINT",EDGE,{"derivedFrom":subQ0}),1.0]])]});}
            var Q40;
            {var subQ1=sQuery(id+"F0.wireOp",EDGE,"E9.3.26.0");Q40=makeQuery(id+"F0.imprint","IMPRINT",FACE,{"disambiguationData":[TD([[makeQuery(id+"F0.imprint","IMPRINT",EDGE,{"derivedFrom":subQ1}),1.0]])]});}
            var Q41;
            {var subQ0=sQuery(id+"F0.wireOp",EDGE,"E9.3.10.0");Q41=makeQuery(id+"F0.imprint","IMPRINT",FACE,{"disambiguationData":[TD([[makeQuery(id+"F0.imprint","IMPRINT",EDGE,{"derivedFrom":subQ0}),1.0]])]});}
            var Q42;
            {var subQ1=sQuery(id+"F0.wireOp",EDGE,"E9.3.43.0");Q42=makeQuery(id+"F0.imprint","IMPRINT",FACE,{"disambiguationData":[TD([[makeQuery(id+"F0.imprint","IMPRINT",EDGE,{"derivedFrom":subQ1}),1.0]])]});}
            var Q43;
            {var subQ1=sQuery(id+"F0.wireOp",EDGE,"E9.3.44.0");Q43=makeQuery(id+"F0.imprint","IMPRINT",FACE,{"disambiguationData":[TD([[makeQuery(id+"F0.imprint","IMPRINT",EDGE,{"derivedFrom":subQ1}),1.0]])]});}
            var Q44;
            {var subQ0=sQuery(id+"F0.wireOp",EDGE,"E1");Q44=makeQuery(id+"F0.imprint","IMPRINT",FACE,{"disambiguationData":[TD([[makeQuery(id+"F0.imprint","IMPRINT",EDGE,{"derivedFrom":subQ0}),1.0]])]});}
            var Q45;
            {var subQ1=sQuery(id+"F0.wireOp",EDGE,"E9.3.58.0");Q45=makeQuery(id+"F0.imprint","IMPRINT",FACE,{"disambiguationData":[TD([[makeQuery(id+"F0.imprint","IMPRINT",EDGE,{"derivedFrom":subQ1}),1.0]])]});}
            var Q46;
            {var subQ1=sQuery(id+"F0.wireOp",EDGE,"E9.3.59.0");Q46=makeQuery(id+"F0.imprint","IMPRINT",FACE,{"disambiguationData":[TD([[makeQuery(id+"F0.imprint","IMPRINT",EDGE,{"derivedFrom":subQ1}),1.0]])]});}
            var Q47;
            {var subQ1=sQuery(id+"F0.wireOp",EDGE,"E9.3.45.0");Q47=makeQuery(id+"F0.imprint","IMPRINT",FACE,{"disambiguationData":[TD([[makeQuery(id+"F0.imprint","IMPRINT",EDGE,{"derivedFrom":subQ1}),1.0]])]});}
            var Q48;
            {var subQ1=sQuery(id+"F0.wireOp",EDGE,"E9.3.46.0");Q48=makeQuery(id+"F0.imprint","IMPRINT",FACE,{"disambiguationData":[TD([[makeQuery(id+"F0.imprint","IMPRINT",EDGE,{"derivedFrom":subQ1}),1.0]])]});}
            var Q49;
            {var subQ0=sQuery(id+"F0.wireOp",EDGE,"E9.3.47.0");Q49=makeQuery(id+"F0.imprint","IMPRINT",FACE,{"disambiguationData":[TD([[makeQuery(id+"F0.imprint","IMPRINT",EDGE,{"derivedFrom":subQ0}),1.0]])]});}
            var Q50;
            {var subQ0=sQuery(id+"F0.wireOp",EDGE,"E9.3.48.0");Q50=makeQuery(id+"F0.imprint","IMPRINT",FACE,{"disambiguationData":[TD([[makeQuery(id+"F0.imprint","IMPRINT",EDGE,{"derivedFrom":subQ0}),1.0]])]});}
            var Q51;
            {var subQ1=sQuery(id+"F0.wireOp",EDGE,"E9.3.49.0");Q51=makeQuery(id+"F0.imprint","IMPRINT",FACE,{"disambiguationData":[TD([[makeQuery(id+"F0.imprint","IMPRINT",EDGE,{"derivedFrom":subQ1}),1.0]])]});}
            var Q52;
            {var subQ1=sQuery(id+"F0.wireOp",EDGE,"E9.3.50.0");Q52=makeQuery(id+"F0.imprint","IMPRINT",FACE,{"disambiguationData":[TD([[makeQuery(id+"F0.imprint","IMPRINT",EDGE,{"derivedFrom":subQ1}),1.0]])]});}
            var Q53;
            {var subQ1=sQuery(id+"F0.wireOp",EDGE,"E9.3.51.0");Q53=makeQuery(id+"F0.imprint","IMPRINT",FACE,{"disambiguationData":[TD([[makeQuery(id+"F0.imprint","IMPRINT",EDGE,{"derivedFrom":subQ1}),1.0]])]});}
            var Q54;
            {var subQ1=sQuery(id+"F0.wireOp",EDGE,"E9.3.52.0");Q54=makeQuery(id+"F0.imprint","IMPRINT",FACE,{"disambiguationData":[TD([[makeQuery(id+"F0.imprint","IMPRINT",EDGE,{"derivedFrom":subQ1}),1.0]])]});}
            var Q55;
            {var subQ1=sQuery(id+"F0.wireOp",EDGE,"E9.3.56.0");Q55=makeQuery(id+"F0.imprint","IMPRINT",FACE,{"disambiguationData":[TD([[makeQuery(id+"F0.imprint","IMPRINT",EDGE,{"derivedFrom":subQ1}),1.0]])]});}
            var Q56;
            {var subQ1=sQuery(id+"F0.wireOp",EDGE,"E9.3.57.0");Q56=makeQuery(id+"F0.imprint","IMPRINT",FACE,{"disambiguationData":[TD([[makeQuery(id+"F0.imprint","IMPRINT",EDGE,{"derivedFrom":subQ1}),1.0]])]});}
            var Q57;
            {var subQ1=sQuery(id+"F0.wireOp",EDGE,"E9.3.18.0");Q57=makeQuery(id+"F0.imprint","IMPRINT",FACE,{"disambiguationData":[TD([[makeQuery(id+"F0.imprint","IMPRINT",EDGE,{"derivedFrom":subQ1}),1.0]])]});}
            var Q58;
            {var subQ1=sQuery(id+"F0.wireOp",EDGE,"E9.3.25.0");Q58=makeQuery(id+"F0.imprint","IMPRINT",FACE,{"disambiguationData":[TD([[makeQuery(id+"F0.imprint","IMPRINT",EDGE,{"derivedFrom":subQ1}),1.0]])]});}
            var Q59;
            {var subQ1=sQuery(id+"F0.wireOp",EDGE,"E9.3.9.0");Q59=makeQuery(id+"F0.imprint","IMPRINT",FACE,{"disambiguationData":[TD([[makeQuery(id+"F0.imprint","IMPRINT",EDGE,{"derivedFrom":subQ1}),1.0]])]});}
            var Q60;
            {var subQ1=sQuery(id+"F0.wireOp",EDGE,"E9.3.11.0");Q60=makeQuery(id+"F0.imprint","IMPRINT",FACE,{"disambiguationData":[TD([[makeQuery(id+"F0.imprint","IMPRINT",EDGE,{"derivedFrom":subQ1}),1.0]])]});}
            extrude(context, id + "F1", {"entities" : qUnion([Q0, Q1, Q2, Q3, Q4, Q5, Q6, Q7, Q8, Q9, Q10, Q11, Q12, Q13, Q14, Q15, Q16, Q17, Q18, Q19, Q20, Q21, Q22, Q23, Q24, Q25, Q26, Q27, Q28, Q29, Q30, Q31, Q32, Q33, Q34, Q35, Q36, Q37, Q38, Q39, Q40, Q41, Q42, Q43, Q44, Q45, Q46, Q47, Q48, Q49, Q50, Q51, Q52, Q53, Q54, Q55, Q56, Q57, Q58, Q59, Q60]), "depth" : 6.35 * mm});
        }
        {
            var Q0;
            Q0=makeQuery(id+"F1.opExtrude","CAP_FACE",FACE,{"disambiguationData":[OSD([sQuery(id+"F0.wireOp",EDGE,"E0"),sQuery(id+"F0.wireOp",EDGE,"E1"),sQuery(id+"F0.wireOp",EDGE,"E3.trimOffspring"),sQuery(id+"F0.wireOp",EDGE,"E4.trimOffspring"),sQuery(id+"F0.wireOp",EDGE,"E5.MirrorCS"),sQuery(id+"F0.wireOp",EDGE,"E6.MirrorCS"),sQuery(id+"F0.wireOp",EDGE,"E7.MirrorCS"),sQuery(id+"F0.wireOp",EDGE,"E8.1.1"),sQuery(id+"F0.wireOp",EDGE,"E8.1.2"),sQuery(id+"F0.wireOp",EDGE,"E8.1.3"),sQuery(id+"F0.wireOp",EDGE,"E8.1.4"),sQuery(id+"F0.wireOp",EDGE,"E8.1.5"),sQuery(id+"F0.wireOp",EDGE,"E8.1.6"),sQuery(id+"F0.wireOp",EDGE,"E8.2.1"),sQuery(id+"F0.wireOp",EDGE,"E8.2.2"),sQuery(id+"F0.wireOp",EDGE,"E8.2.3"),sQuery(id+"F0.wireOp",EDGE,"E8.2.4"),sQuery(id+"F0.wireOp",EDGE,"E8.2.5"),sQuery(id+"F0.wireOp",EDGE,"E8.2.6"),sQuery(id+"F0.wireOp",EDGE,"E9.3.3.0"),sQuery(id+"F0.wireOp",EDGE,"E9.6.3.0"),sQuery(id+"F0.wireOp",EDGE,"E9.9.3.0"),sQuery(id+"F0.wireOp",EDGE,"E9.13.3.0"),sQuery(id+"F0.wireOp",EDGE,"E9.17.3.0"),sQuery(id+"F0.wireOp",EDGE,"E9.21.3.0"),sQuery(id+"F0.wireOp",EDGE,"E9.3.4.0"),sQuery(id+"F0.wireOp",EDGE,"E9.6.4.0"),sQuery(id+"F0.wireOp",EDGE,"E9.9.4.0"),sQuery(id+"F0.wireOp",EDGE,"E9.13.4.0"),sQuery(id+"F0.wireOp",EDGE,"E9.17.4.0"),sQuery(id+"F0.wireOp",EDGE,"E9.21.4.0"),sQuery(id+"F0.wireOp",EDGE,"E9.3.5.0"),sQuery(id+"F0.wireOp",EDGE,"E9.6.5.0"),sQuery(id+"F0.wireOp",EDGE,"E9.9.5.0"),sQuery(id+"F0.wireOp",EDGE,"E9.13.5.0"),sQuery(id+"F0.wireOp",EDGE,"E9.17.5.0"),sQuery(id+"F0.wireOp",EDGE,"E9.21.5.0"),sQuery(id+"F0.wireOp",EDGE,"E9.3.6.0"),sQuery(id+"F0.wireOp",EDGE,"E9.6.6.0"),sQuery(id+"F0.wireOp",EDGE,"E9.9.6.0"),sQuery(id+"F0.wireOp",EDGE,"E9.13.6.0"),sQuery(id+"F0.wireOp",EDGE,"E9.17.6.0"),sQuery(id+"F0.wireOp",EDGE,"E9.21.6.0"),sQuery(id+"F0.wireOp",EDGE,"E9.3.7.0"),sQuery(id+"F0.wireOp",EDGE,"E9.6.7.0"),sQuery(id+"F0.wireOp",EDGE,"E9.9.7.0"),sQuery(id+"F0.wireOp",EDGE,"E9.13.7.0"),sQuery(id+"F0.wireOp",EDGE,"E9.17.7.0"),sQuery(id+"F0.wireOp",EDGE,"E9.21.7.0"),sQuery(id+"F0.wireOp",EDGE,"E9.3.8.0"),sQuery(id+"F0.wireOp",EDGE,"E9.6.8.0"),sQuery(id+"F0.wireOp",EDGE,"E9.9.8.0"),sQuery(id+"F0.wireOp",EDGE,"E9.13.8.0"),sQuery(id+"F0.wireOp",EDGE,"E9.17.8.0"),sQuery(id+"F0.wireOp",EDGE,"E9.21.8.0"),sQuery(id+"F0.wireOp",EDGE,"E9.3.9.0"),sQuery(id+"F0.wireOp",EDGE,"E9.6.9.0"),sQuery(id+"F0.wireOp",EDGE,"E9.9.9.0"),sQuery(id+"F0.wireOp",EDGE,"E9.13.9.0"),sQuery(id+"F0.wireOp",EDGE,"E9.17.9.0"),sQuery(id+"F0.wireOp",EDGE,"E9.21.9.0"),sQuery(id+"F0.wireOp",EDGE,"E9.3.10.0"),sQuery(id+"F0.wireOp",EDGE,"E9.6.10.0"),sQuery(id+"F0.wireOp",EDGE,"E9.9.10.0"),sQuery(id+"F0.wireOp",EDGE,"E9.13.10.0"),sQuery(id+"F0.wireOp",EDGE,"E9.17.10.0"),sQuery(id+"F0.wireOp",EDGE,"E9.21.10.0"),sQuery(id+"F0.wireOp",EDGE,"E9.3.11.0"),sQuery(id+"F0.wireOp",EDGE,"E9.6.11.0"),sQuery(id+"F0.wireOp",EDGE,"E9.9.11.0"),sQuery(id+"F0.wireOp",EDGE,"E9.13.11.0"),sQuery(id+"F0.wireOp",EDGE,"E9.17.11.0"),sQuery(id+"F0.wireOp",EDGE,"E9.21.11.0"),sQuery(id+"F0.wireOp",EDGE,"E9.3.12.0"),sQuery(id+"F0.wireOp",EDGE,"E9.6.12.0"),sQuery(id+"F0.wireOp",EDGE,"E9.9.12.0"),sQuery(id+"F0.wireOp",EDGE,"E9.13.12.0"),sQuery(id+"F0.wireOp",EDGE,"E9.17.12.0"),sQuery(id+"F0.wireOp",EDGE,"E9.21.12.0"),sQuery(id+"F0.wireOp",EDGE,"E9.3.13.0"),sQuery(id+"F0.wireOp",EDGE,"E9.6.13.0"),sQuery(id+"F0.wireOp",EDGE,"E9.9.13.0"),sQuery(id+"F0.wireOp",EDGE,"E9.13.13.0"),sQuery(id+"F0.wireOp",EDGE,"E9.17.13.0"),sQuery(id+"F0.wireOp",EDGE,"E9.21.13.0"),sQuery(id+"F0.wireOp",EDGE,"E9.3.14.0"),sQuery(id+"F0.wireOp",EDGE,"E9.6.14.0"),sQuery(id+"F0.wireOp",EDGE,"E9.9.14.0"),sQuery(id+"F0.wireOp",EDGE,"E9.13.14.0"),sQuery(id+"F0.wireOp",EDGE,"E9.17.14.0"),sQuery(id+"F0.wireOp",EDGE,"E9.21.14.0"),sQuery(id+"F0.wireOp",EDGE,"E9.3.15.0"),sQuery(id+"F0.wireOp",EDGE,"E9.6.15.0"),sQuery(id+"F0.wireOp",EDGE,"E9.9.15.0"),sQuery(id+"F0.wireOp",EDGE,"E9.13.15.0"),sQuery(id+"F0.wireOp",EDGE,"E9.17.15.0"),sQuery(id+"F0.wireOp",EDGE,"E9.21.15.0"),sQuery(id+"F0.wireOp",EDGE,"E9.3.16.0"),sQuery(id+"F0.wireOp",EDGE,"E9.6.16.0"),sQuery(id+"F0.wireOp",EDGE,"E9.9.16.0"),sQuery(id+"F0.wireOp",EDGE,"E9.13.16.0"),sQuery(id+"F0.wireOp",EDGE,"E9.17.16.0"),sQuery(id+"F0.wireOp",EDGE,"E9.21.16.0"),sQuery(id+"F0.wireOp",EDGE,"E9.3.17.0"),sQuery(id+"F0.wireOp",EDGE,"E9.6.17.0"),sQuery(id+"F0.wireOp",EDGE,"E9.9.17.0"),sQuery(id+"F0.wireOp",EDGE,"E9.13.17.0"),sQuery(id+"F0.wireOp",EDGE,"E9.17.17.0"),sQuery(id+"F0.wireOp",EDGE,"E9.21.17.0"),sQuery(id+"F0.wireOp",EDGE,"E9.3.18.0"),sQuery(id+"F0.wireOp",EDGE,"E9.6.18.0"),sQuery(id+"F0.wireOp",EDGE,"E9.9.18.0"),sQuery(id+"F0.wireOp",EDGE,"E9.13.18.0"),sQuery(id+"F0.wireOp",EDGE,"E9.17.18.0"),sQuery(id+"F0.wireOp",EDGE,"E9.21.18.0"),sQuery(id+"F0.wireOp",EDGE,"E9.3.19.0"),sQuery(id+"F0.wireOp",EDGE,"E9.6.19.0"),sQuery(id+"F0.wireOp",EDGE,"E9.9.19.0"),sQuery(id+"F0.wireOp",EDGE,"E9.13.19.0"),sQuery(id+"F0.wireOp",EDGE,"E9.17.19.0"),sQuery(id+"F0.wireOp",EDGE,"E9.21.19.0"),sQuery(id+"F0.wireOp",EDGE,"E9.3.20.0"),sQuery(id+"F0.wireOp",EDGE,"E9.6.20.0"),sQuery(id+"F0.wireOp",EDGE,"E9.9.20.0"),sQuery(id+"F0.wireOp",EDGE,"E9.13.20.0"),sQuery(id+"F0.wireOp",EDGE,"E9.17.20.0"),sQuery(id+"F0.wireOp",EDGE,"E9.21.20.0"),sQuery(id+"F0.wireOp",EDGE,"E9.3.21.0"),sQuery(id+"F0.wireOp",EDGE,"E9.6.21.0"),sQuery(id+"F0.wireOp",EDGE,"E9.9.21.0"),sQuery(id+"F0.wireOp",EDGE,"E9.13.21.0"),sQuery(id+"F0.wireOp",EDGE,"E9.17.21.0"),sQuery(id+"F0.wireOp",EDGE,"E9.21.21.0"),sQuery(id+"F0.wireOp",EDGE,"E9.3.22.0"),sQuery(id+"F0.wireOp",EDGE,"E9.6.22.0"),sQuery(id+"F0.wireOp",EDGE,"E9.9.22.0"),sQuery(id+"F0.wireOp",EDGE,"E9.13.22.0"),sQuery(id+"F0.wireOp",EDGE,"E9.17.22.0"),sQuery(id+"F0.wireOp",EDGE,"E9.21.22.0"),sQuery(id+"F0.wireOp",EDGE,"E9.3.23.0"),sQuery(id+"F0.wireOp",EDGE,"E9.6.23.0"),sQuery(id+"F0.wireOp",EDGE,"E9.9.23.0"),sQuery(id+"F0.wireOp",EDGE,"E9.13.23.0"),sQuery(id+"F0.wireOp",EDGE,"E9.17.23.0"),sQuery(id+"F0.wireOp",EDGE,"E9.21.23.0"),sQuery(id+"F0.wireOp",EDGE,"E9.3.24.0"),sQuery(id+"F0.wireOp",EDGE,"E9.6.24.0"),sQuery(id+"F0.wireOp",EDGE,"E9.9.24.0"),sQuery(id+"F0.wireOp",EDGE,"E9.13.24.0"),sQuery(id+"F0.wireOp",EDGE,"E9.17.24.0"),sQuery(id+"F0.wireOp",EDGE,"E9.21.24.0"),sQuery(id+"F0.wireOp",EDGE,"E9.3.25.0"),sQuery(id+"F0.wireOp",EDGE,"E9.6.25.0"),sQuery(id+"F0.wireOp",EDGE,"E9.9.25.0"),sQuery(id+"F0.wireOp",EDGE,"E9.13.25.0"),sQuery(id+"F0.wireOp",EDGE,"E9.17.25.0"),sQuery(id+"F0.wireOp",EDGE,"E9.21.25.0"),sQuery(id+"F0.wireOp",EDGE,"E9.3.26.0"),sQuery(id+"F0.wireOp",EDGE,"E9.6.26.0"),sQuery(id+"F0.wireOp",EDGE,"E9.9.26.0"),sQuery(id+"F0.wireOp",EDGE,"E9.13.26.0"),sQuery(id+"F0.wireOp",EDGE,"E9.17.26.0"),sQuery(id+"F0.wireOp",EDGE,"E9.21.26.0"),sQuery(id+"F0.wireOp",EDGE,"E9.3.27.0"),sQuery(id+"F0.wireOp",EDGE,"E9.6.27.0"),sQuery(id+"F0.wireOp",EDGE,"E9.9.27.0"),sQuery(id+"F0.wireOp",EDGE,"E9.13.27.0"),sQuery(id+"F0.wireOp",EDGE,"E9.17.27.0"),sQuery(id+"F0.wireOp",EDGE,"E9.21.27.0"),sQuery(id+"F0.wireOp",EDGE,"E9.3.28.0"),sQuery(id+"F0.wireOp",EDGE,"E9.6.28.0"),sQuery(id+"F0.wireOp",EDGE,"E9.9.28.0"),sQuery(id+"F0.wireOp",EDGE,"E9.13.28.0"),sQuery(id+"F0.wireOp",EDGE,"E9.17.28.0"),sQuery(id+"F0.wireOp",EDGE,"E9.21.28.0"),sQuery(id+"F0.wireOp",EDGE,"E9.3.29.0"),sQuery(id+"F0.wireOp",EDGE,"E9.6.29.0"),sQuery(id+"F0.wireOp",EDGE,"E9.9.29.0"),sQuery(id+"F0.wireOp",EDGE,"E9.13.29.0"),sQuery(id+"F0.wireOp",EDGE,"E9.17.29.0"),sQuery(id+"F0.wireOp",EDGE,"E9.21.29.0"),sQuery(id+"F0.wireOp",EDGE,"E9.3.30.0"),sQuery(id+"F0.wireOp",EDGE,"E9.6.30.0"),sQuery(id+"F0.wireOp",EDGE,"E9.9.30.0"),sQuery(id+"F0.wireOp",EDGE,"E9.13.30.0"),sQuery(id+"F0.wireOp",EDGE,"E9.17.30.0"),sQuery(id+"F0.wireOp",EDGE,"E9.21.30.0"),sQuery(id+"F0.wireOp",EDGE,"E9.3.31.0"),sQuery(id+"F0.wireOp",EDGE,"E9.6.31.0"),sQuery(id+"F0.wireOp",EDGE,"E9.9.31.0"),sQuery(id+"F0.wireOp",EDGE,"E9.13.31.0"),sQuery(id+"F0.wireOp",EDGE,"E9.17.31.0"),sQuery(id+"F0.wireOp",EDGE,"E9.21.31.0"),sQuery(id+"F0.wireOp",EDGE,"E9.3.32.0"),sQuery(id+"F0.wireOp",EDGE,"E9.6.32.0"),sQuery(id+"F0.wireOp",EDGE,"E9.9.32.0"),sQuery(id+"F0.wireOp",EDGE,"E9.13.32.0"),sQuery(id+"F0.wireOp",EDGE,"E9.17.32.0"),sQuery(id+"F0.wireOp",EDGE,"E9.21.32.0"),sQuery(id+"F0.wireOp",EDGE,"E9.3.33.0"),sQuery(id+"F0.wireOp",EDGE,"E9.6.33.0"),sQuery(id+"F0.wireOp",EDGE,"E9.9.33.0"),sQuery(id+"F0.wireOp",EDGE,"E9.13.33.0"),sQuery(id+"F0.wireOp",EDGE,"E9.17.33.0"),sQuery(id+"F0.wireOp",EDGE,"E9.21.33.0"),sQuery(id+"F0.wireOp",EDGE,"E9.3.34.0"),sQuery(id+"F0.wireOp",EDGE,"E9.6.34.0"),sQuery(id+"F0.wireOp",EDGE,"E9.9.34.0"),sQuery(id+"F0.wireOp",EDGE,"E9.13.34.0"),sQuery(id+"F0.wireOp",EDGE,"E9.17.34.0"),sQuery(id+"F0.wireOp",EDGE,"E9.21.34.0"),sQuery(id+"F0.wireOp",EDGE,"E9.3.35.0"),sQuery(id+"F0.wireOp",EDGE,"E9.6.35.0"),sQuery(id+"F0.wireOp",EDGE,"E9.9.35.0"),sQuery(id+"F0.wireOp",EDGE,"E9.13.35.0"),sQuery(id+"F0.wireOp",EDGE,"E9.17.35.0"),sQuery(id+"F0.wireOp",EDGE,"E9.21.35.0"),sQuery(id+"F0.wireOp",EDGE,"E9.3.36.0"),sQuery(id+"F0.wireOp",EDGE,"E9.6.36.0"),sQuery(id+"F0.wireOp",EDGE,"E9.9.36.0"),sQuery(id+"F0.wireOp",EDGE,"E9.13.36.0"),sQuery(id+"F0.wireOp",EDGE,"E9.17.36.0"),sQuery(id+"F0.wireOp",EDGE,"E9.21.36.0"),sQuery(id+"F0.wireOp",EDGE,"E9.3.37.0"),sQuery(id+"F0.wireOp",EDGE,"E9.6.37.0"),sQuery(id+"F0.wireOp",EDGE,"E9.9.37.0"),sQuery(id+"F0.wireOp",EDGE,"E9.13.37.0"),sQuery(id+"F0.wireOp",EDGE,"E9.17.37.0"),sQuery(id+"F0.wireOp",EDGE,"E9.21.37.0"),sQuery(id+"F0.wireOp",EDGE,"E9.3.38.0"),sQuery(id+"F0.wireOp",EDGE,"E9.6.38.0"),sQuery(id+"F0.wireOp",EDGE,"E9.9.38.0"),sQuery(id+"F0.wireOp",EDGE,"E9.13.38.0"),sQuery(id+"F0.wireOp",EDGE,"E9.17.38.0"),sQuery(id+"F0.wireOp",EDGE,"E9.21.38.0"),sQuery(id+"F0.wireOp",EDGE,"E9.3.39.0"),sQuery(id+"F0.wireOp",EDGE,"E9.6.39.0"),sQuery(id+"F0.wireOp",EDGE,"E9.9.39.0"),sQuery(id+"F0.wireOp",EDGE,"E9.13.39.0"),sQuery(id+"F0.wireOp",EDGE,"E9.17.39.0"),sQuery(id+"F0.wireOp",EDGE,"E9.21.39.0"),sQuery(id+"F0.wireOp",EDGE,"E9.3.40.0"),sQuery(id+"F0.wireOp",EDGE,"E9.6.40.0"),sQuery(id+"F0.wireOp",EDGE,"E9.9.40.0"),sQuery(id+"F0.wireOp",EDGE,"E9.13.40.0"),sQuery(id+"F0.wireOp",EDGE,"E9.17.40.0"),sQuery(id+"F0.wireOp",EDGE,"E9.21.40.0"),sQuery(id+"F0.wireOp",EDGE,"E9.3.41.0"),sQuery(id+"F0.wireOp",EDGE,"E9.6.41.0"),sQuery(id+"F0.wireOp",EDGE,"E9.9.41.0"),sQuery(id+"F0.wireOp",EDGE,"E9.13.41.0"),sQuery(id+"F0.wireOp",EDGE,"E9.17.41.0"),sQuery(id+"F0.wireOp",EDGE,"E9.21.41.0"),sQuery(id+"F0.wireOp",EDGE,"E9.3.42.0"),sQuery(id+"F0.wireOp",EDGE,"E9.6.42.0"),sQuery(id+"F0.wireOp",EDGE,"E9.9.42.0"),sQuery(id+"F0.wireOp",EDGE,"E9.13.42.0"),sQuery(id+"F0.wireOp",EDGE,"E9.17.42.0"),sQuery(id+"F0.wireOp",EDGE,"E9.21.42.0"),sQuery(id+"F0.wireOp",EDGE,"E9.3.43.0"),sQuery(id+"F0.wireOp",EDGE,"E9.6.43.0"),sQuery(id+"F0.wireOp",EDGE,"E9.9.43.0"),sQuery(id+"F0.wireOp",EDGE,"E9.13.43.0"),sQuery(id+"F0.wireOp",EDGE,"E9.17.43.0"),sQuery(id+"F0.wireOp",EDGE,"E9.21.43.0"),sQuery(id+"F0.wireOp",EDGE,"E9.3.44.0"),sQuery(id+"F0.wireOp",EDGE,"E9.6.44.0"),sQuery(id+"F0.wireOp",EDGE,"E9.9.44.0"),sQuery(id+"F0.wireOp",EDGE,"E9.13.44.0"),sQuery(id+"F0.wireOp",EDGE,"E9.17.44.0"),sQuery(id+"F0.wireOp",EDGE,"E9.21.44.0"),sQuery(id+"F0.wireOp",EDGE,"E9.3.45.0"),sQuery(id+"F0.wireOp",EDGE,"E9.6.45.0"),sQuery(id+"F0.wireOp",EDGE,"E9.9.45.0"),sQuery(id+"F0.wireOp",EDGE,"E9.13.45.0"),sQuery(id+"F0.wireOp",EDGE,"E9.17.45.0"),sQuery(id+"F0.wireOp",EDGE,"E9.21.45.0"),sQuery(id+"F0.wireOp",EDGE,"E9.3.46.0"),sQuery(id+"F0.wireOp",EDGE,"E9.6.46.0"),sQuery(id+"F0.wireOp",EDGE,"E9.9.46.0"),sQuery(id+"F0.wireOp",EDGE,"E9.13.46.0"),sQuery(id+"F0.wireOp",EDGE,"E9.17.46.0"),sQuery(id+"F0.wireOp",EDGE,"E9.21.46.0"),sQuery(id+"F0.wireOp",EDGE,"E9.3.47.0"),sQuery(id+"F0.wireOp",EDGE,"E9.6.47.0"),sQuery(id+"F0.wireOp",EDGE,"E9.9.47.0"),sQuery(id+"F0.wireOp",EDGE,"E9.13.47.0"),sQuery(id+"F0.wireOp",EDGE,"E9.17.47.0"),sQuery(id+"F0.wireOp",EDGE,"E9.21.47.0"),sQuery(id+"F0.wireOp",EDGE,"E9.3.48.0"),sQuery(id+"F0.wireOp",EDGE,"E9.6.48.0"),sQuery(id+"F0.wireOp",EDGE,"E9.9.48.0"),sQuery(id+"F0.wireOp",EDGE,"E9.13.48.0"),sQuery(id+"F0.wireOp",EDGE,"E9.17.48.0"),sQuery(id+"F0.wireOp",EDGE,"E9.21.48.0"),sQuery(id+"F0.wireOp",EDGE,"E9.3.49.0"),sQuery(id+"F0.wireOp",EDGE,"E9.6.49.0"),sQuery(id+"F0.wireOp",EDGE,"E9.9.49.0"),sQuery(id+"F0.wireOp",EDGE,"E9.13.49.0"),sQuery(id+"F0.wireOp",EDGE,"E9.17.49.0"),sQuery(id+"F0.wireOp",EDGE,"E9.21.49.0"),sQuery(id+"F0.wireOp",EDGE,"E9.3.50.0"),sQuery(id+"F0.wireOp",EDGE,"E9.6.50.0"),sQuery(id+"F0.wireOp",EDGE,"E9.9.50.0"),sQuery(id+"F0.wireOp",EDGE,"E9.13.50.0"),sQuery(id+"F0.wireOp",EDGE,"E9.17.50.0"),sQuery(id+"F0.wireOp",EDGE,"E9.21.50.0"),sQuery(id+"F0.wireOp",EDGE,"E9.3.51.0"),sQuery(id+"F0.wireOp",EDGE,"E9.6.51.0"),sQuery(id+"F0.wireOp",EDGE,"E9.9.51.0"),sQuery(id+"F0.wireOp",EDGE,"E9.13.51.0"),sQuery(id+"F0.wireOp",EDGE,"E9.17.51.0"),sQuery(id+"F0.wireOp",EDGE,"E9.21.51.0"),sQuery(id+"F0.wireOp",EDGE,"E9.3.52.0"),sQuery(id+"F0.wireOp",EDGE,"E9.6.52.0"),sQuery(id+"F0.wireOp",EDGE,"E9.9.52.0"),sQuery(id+"F0.wireOp",EDGE,"E9.13.52.0"),sQuery(id+"F0.wireOp",EDGE,"E9.17.52.0"),sQuery(id+"F0.wireOp",EDGE,"E9.21.52.0"),sQuery(id+"F0.wireOp",EDGE,"E9.3.53.0"),sQuery(id+"F0.wireOp",EDGE,"E9.6.53.0"),sQuery(id+"F0.wireOp",EDGE,"E9.9.53.0"),sQuery(id+"F0.wireOp",EDGE,"E9.13.53.0"),sQuery(id+"F0.wireOp",EDGE,"E9.17.53.0"),sQuery(id+"F0.wireOp",EDGE,"E9.21.53.0"),sQuery(id+"F0.wireOp",EDGE,"E9.3.54.0"),sQuery(id+"F0.wireOp",EDGE,"E9.6.54.0"),sQuery(id+"F0.wireOp",EDGE,"E9.9.54.0"),sQuery(id+"F0.wireOp",EDGE,"E9.13.54.0"),sQuery(id+"F0.wireOp",EDGE,"E9.17.54.0"),sQuery(id+"F0.wireOp",EDGE,"E9.21.54.0"),sQuery(id+"F0.wireOp",EDGE,"E9.3.55.0"),sQuery(id+"F0.wireOp",EDGE,"E9.6.55.0"),sQuery(id+"F0.wireOp",EDGE,"E9.9.55.0"),sQuery(id+"F0.wireOp",EDGE,"E9.13.55.0"),sQuery(id+"F0.wireOp",EDGE,"E9.17.55.0"),sQuery(id+"F0.wireOp",EDGE,"E9.21.55.0"),sQuery(id+"F0.wireOp",EDGE,"E9.3.56.0"),sQuery(id+"F0.wireOp",EDGE,"E9.6.56.0"),sQuery(id+"F0.wireOp",EDGE,"E9.9.56.0"),sQuery(id+"F0.wireOp",EDGE,"E9.13.56.0"),sQuery(id+"F0.wireOp",EDGE,"E9.17.56.0"),sQuery(id+"F0.wireOp",EDGE,"E9.21.56.0"),sQuery(id+"F0.wireOp",EDGE,"E9.3.57.0"),sQuery(id+"F0.wireOp",EDGE,"E9.6.57.0"),sQuery(id+"F0.wireOp",EDGE,"E9.9.57.0"),sQuery(id+"F0.wireOp",EDGE,"E9.13.57.0"),sQuery(id+"F0.wireOp",EDGE,"E9.17.57.0"),sQuery(id+"F0.wireOp",EDGE,"E9.21.57.0"),sQuery(id+"F0.wireOp",EDGE,"E9.3.58.0"),sQuery(id+"F0.wireOp",EDGE,"E9.6.58.0"),sQuery(id+"F0.wireOp",EDGE,"E9.9.58.0"),sQuery(id+"F0.wireOp",EDGE,"E9.13.58.0"),sQuery(id+"F0.wireOp",EDGE,"E9.17.58.0"),sQuery(id+"F0.wireOp",EDGE,"E9.21.58.0"),sQuery(id+"F0.wireOp",EDGE,"E9.3.59.0"),sQuery(id+"F0.wireOp",EDGE,"E9.6.59.0"),sQuery(id+"F0.wireOp",EDGE,"E9.9.59.0"),sQuery(id+"F0.wireOp",EDGE,"E9.13.59.0"),sQuery(id+"F0.wireOp",EDGE,"E9.17.59.0"),sQuery(id+"F0.wireOp",EDGE,"E9.21.59.0")])],"isStart":false});
            var sketch = newSketch(context, id + "F2", { "sketchPlane" : qUnion([Q0])});
            skCircle(sketch, "E10", {"center": v(0, 0) * mm, "radius": 11.43 * mm});
            skSolve(sketch);
        }
        {
            var Q0;
            Q0=makeQuery(id+"F2.imprint","IMPRINT",FACE,{"disambiguationData":[TD([[makeQuery(id+"F2.imprint","IMPRINT",EDGE,{"derivedFrom":sQuery(id+"F2.wireOp",EDGE,"E10")}),1.0]])]});
            extrude(context, id + "F3", {"entities" : qUnion([Q0]), "operationType" : NewBodyOperationType.ADD, "depth" : 7.37 * mm});
        }
        {
            var Q0;
            Q0=makeQuery(id+"F3.opExtrude","CAP_FACE",FACE,{"disambiguationData":[OSD([sQuery(id+"F2.wireOp",EDGE,"E10")])],"isStart":false});
            var sketch = newSketch(context, id + "F4", { "sketchPlane" : qUnion([Q0])});
            skCircle(sketch, "E11.cCircle", {"center": v(0, 0) * mm, "radius": 5.56 * mm, "construction": true});
            skLineSegment(sketch, "E11.0", {"start": v(5.56, 0) * mm, "end": v(2.78, -4.81) * mm});
            skLineSegment(sketch, "E11.1", {"start": v(2.78, -4.81) * mm, "end": v(-2.78, -4.81) * mm});
            skLineSegment(sketch, "E11.2", {"start": v(-2.78, -4.81) * mm, "end": v(-5.56, 0) * mm});
            skLineSegment(sketch, "E11.3", {"start": v(-5.56, 0) * mm, "end": v(-2.78, 4.81) * mm});
            skLineSegment(sketch, "E11.4", {"start": v(-2.78, 4.81) * mm, "end": v(2.78, 4.81) * mm});
            skLineSegment(sketch, "E11.5", {"start": v(2.78, 4.81) * mm, "end": v(5.56, 0) * mm});
            skSolve(sketch);
        }
        {
            var Q0;
            Q0=makeQuery(id+"F4.imprint","IMPRINT",FACE,{"disambiguationData":[TD([[makeQuery(id+"F4.imprint","IMPRINT",EDGE,{"derivedFrom":sQuery(id+"F4.wireOp",EDGE,"E11.0")}),-1.0]])]});
            extrude(context, id + "F5", {"entities" : qUnion([Q0]), "operationType" : NewBodyOperationType.REMOVE, "oppositeDirection" : true, "depth" : 25.4 * mm});
        }
    });
